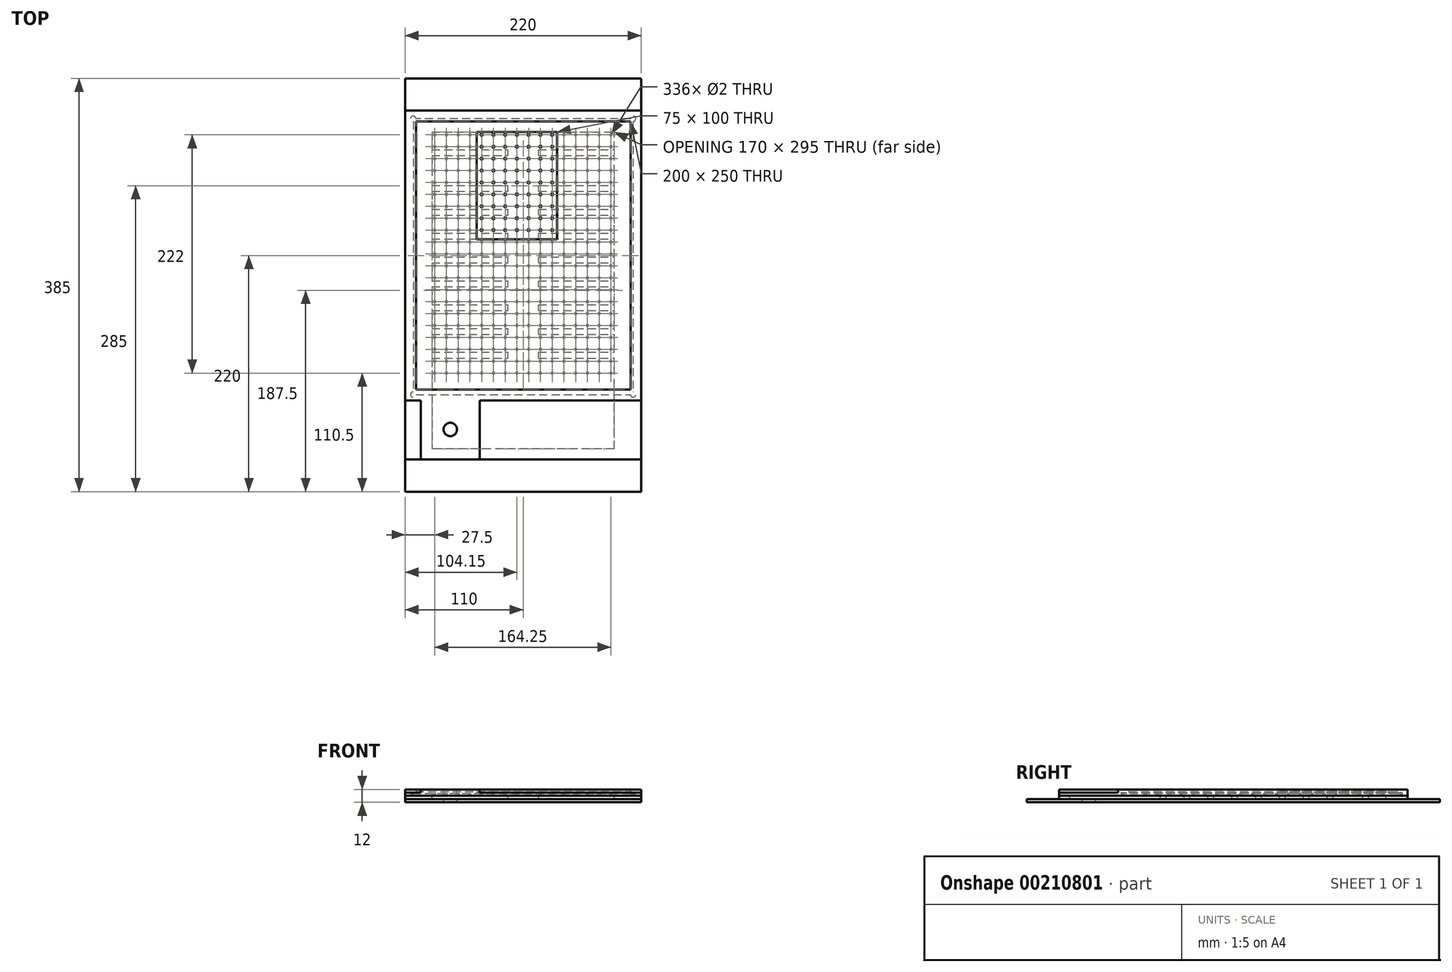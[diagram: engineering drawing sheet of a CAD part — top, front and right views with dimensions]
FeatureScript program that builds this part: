
annotation { "Feature Type Name" : "Feature", "Feature Type Description" : "" }
export const myFeature = defineFeature(function(context is Context, id is Id, definition is map)
    precondition{}
    {
        {
            var Q0;
            Q0=qCreatedBy(makeId("Top.planeOp"),FACE);
            var sketch = newSketch(context, id + "F0", { "sketchPlane" : qUnion([Q0])});
            skLineSegment(sketch, "E0.bottom", {"start": v(0, 0) * mm, "end": v(200, 0) * mm});
            skLineSegment(sketch, "E0.top", {"start": v(0, 250) * mm, "end": v(200, 250) * mm});
            skLineSegment(sketch, "E0.left", {"start": v(0, 0) * mm, "end": v(0, 250) * mm});
            skLineSegment(sketch, "E0.right", {"start": v(200, 0) * mm, "end": v(200, 250) * mm});
            skLineSegment(sketch, "E1.0", {"start": v(-10, -10) * mm, "end": v(-10, 260) * mm});
            skLineSegment(sketch, "E1.1", {"start": v(-10, -10) * mm, "end": v(210, -10) * mm});
            skLineSegment(sketch, "E1.2", {"start": v(210, -10) * mm, "end": v(210, 260) * mm});
            skLineSegment(sketch, "E1.3", {"start": v(-10, 260) * mm, "end": v(210, 260) * mm});
            skSolve(sketch);
        }
        {
            var Q0;
            Q0=makeQuery(id+"F0.imprint","IMPRINT",FACE,{"disambiguationData":[TD([[makeQuery(id+"F0.imprint","IMPRINT",EDGE,{"derivedFrom":sQuery(id+"F0.wireOp",EDGE,"E0.bottom")}),-1.0]])]});
            extrude(context, id + "F1", {"entities" : qUnion([Q0]), "depth" : 3 * mm});
        }
        {
            var Q0;
            Q0=qCreatedBy(makeId("Top.planeOp"),FACE);
            var sketch = newSketch(context, id + "F2", { "sketchPlane" : qUnion([Q0])});
            skLineSegment(sketch, "E2.0", {"start": v(-10, 260) * mm, "end": v(210, 260) * mm});
            skLineSegment(sketch, "E3", {"start": v(210, 260) * mm, "end": v(210, -65) * mm});
            skLineSegment(sketch, "E4", {"start": v(210, -65) * mm, "end": v(-10, -65) * mm});
            skLineSegment(sketch, "E5", {"start": v(-10, -65) * mm, "end": v(-10, 260) * mm});
            skLineSegment(sketch, "E6.bottom", {"start": v(15, 240) * mm, "end": v(185, 240) * mm, "construction": true});
            skLineSegment(sketch, "E6.top", {"start": v(15, 10) * mm, "end": v(185, 10) * mm, "construction": true});
            skLineSegment(sketch, "E6.left", {"start": v(15, 240) * mm, "end": v(15, 10) * mm, "construction": true});
            skLineSegment(sketch, "E6.right", {"start": v(185, 240) * mm, "end": v(185, 10) * mm, "construction": true});
            skCircle(sketch, "E7", {"center": v(17.5, 237.5) * mm, "radius": 2.5 * mm});
            skCircle(sketch, "E8.0.1.0", {"center": v(17.5, 226.4) * mm, "radius": 2.5 * mm});
            skCircle(sketch, "E8.0.2.0", {"center": v(17.5, 215.3) * mm, "radius": 2.5 * mm});
            skCircle(sketch, "E8.0.3.0", {"center": v(17.5, 204.2) * mm, "radius": 2.5 * mm});
            skCircle(sketch, "E8.0.4.0", {"center": v(17.5, 193.1) * mm, "radius": 2.5 * mm});
            skCircle(sketch, "E8.0.5.0", {"center": v(17.5, 182) * mm, "radius": 2.5 * mm});
            skCircle(sketch, "E8.0.6.0", {"center": v(17.5, 170.9) * mm, "radius": 2.5 * mm});
            skCircle(sketch, "E8.0.7.0", {"center": v(17.5, 159.8) * mm, "radius": 2.5 * mm});
            skCircle(sketch, "E8.0.8.0", {"center": v(17.5, 148.7) * mm, "radius": 2.5 * mm});
            skCircle(sketch, "E8.0.9.0", {"center": v(17.5, 137.6) * mm, "radius": 2.5 * mm});
            skCircle(sketch, "E8.0.10.0", {"center": v(17.5, 126.5) * mm, "radius": 2.5 * mm});
            skCircle(sketch, "E8.0.11.0", {"center": v(17.5, 115.4) * mm, "radius": 2.5 * mm});
            skCircle(sketch, "E8.0.12.0", {"center": v(17.5, 104.3) * mm, "radius": 2.5 * mm});
            skCircle(sketch, "E8.0.13.0", {"center": v(17.5, 93.2) * mm, "radius": 2.5 * mm});
            skCircle(sketch, "E8.0.14.0", {"center": v(17.5, 82.1) * mm, "radius": 2.5 * mm});
            skCircle(sketch, "E8.0.15.0", {"center": v(17.5, 71) * mm, "radius": 2.5 * mm});
            skCircle(sketch, "E8.0.16.0", {"center": v(17.5, 59.9) * mm, "radius": 2.5 * mm});
            skCircle(sketch, "E8.0.17.0", {"center": v(17.5, 48.8) * mm, "radius": 2.5 * mm});
            skCircle(sketch, "E8.0.18.0", {"center": v(17.5, 37.7) * mm, "radius": 2.5 * mm});
            skCircle(sketch, "E8.0.19.0", {"center": v(17.5, 26.6) * mm, "radius": 2.5 * mm});
            skCircle(sketch, "E8.1.0.0", {"center": v(28.45, 237.5) * mm, "radius": 2.5 * mm});
            skCircle(sketch, "E8.1.1.0", {"center": v(28.45, 226.4) * mm, "radius": 2.5 * mm});
            skCircle(sketch, "E8.1.2.0", {"center": v(28.45, 215.3) * mm, "radius": 2.5 * mm});
            skCircle(sketch, "E8.1.3.0", {"center": v(28.45, 204.2) * mm, "radius": 2.5 * mm});
            skCircle(sketch, "E8.1.4.0", {"center": v(28.45, 193.1) * mm, "radius": 2.5 * mm});
            skCircle(sketch, "E8.1.5.0", {"center": v(28.45, 182) * mm, "radius": 2.5 * mm});
            skCircle(sketch, "E8.1.6.0", {"center": v(28.45, 170.9) * mm, "radius": 2.5 * mm});
            skCircle(sketch, "E8.1.7.0", {"center": v(28.45, 159.8) * mm, "radius": 2.5 * mm});
            skCircle(sketch, "E8.1.8.0", {"center": v(28.45, 148.7) * mm, "radius": 2.5 * mm});
            skCircle(sketch, "E8.1.9.0", {"center": v(28.45, 137.6) * mm, "radius": 2.5 * mm});
            skCircle(sketch, "E8.1.10.0", {"center": v(28.45, 126.5) * mm, "radius": 2.5 * mm});
            skCircle(sketch, "E8.1.11.0", {"center": v(28.45, 115.4) * mm, "radius": 2.5 * mm});
            skCircle(sketch, "E8.1.12.0", {"center": v(28.45, 104.3) * mm, "radius": 2.5 * mm});
            skCircle(sketch, "E8.1.13.0", {"center": v(28.45, 93.2) * mm, "radius": 2.5 * mm});
            skCircle(sketch, "E8.1.14.0", {"center": v(28.45, 82.1) * mm, "radius": 2.5 * mm});
            skCircle(sketch, "E8.1.15.0", {"center": v(28.45, 71) * mm, "radius": 2.5 * mm});
            skCircle(sketch, "E8.1.16.0", {"center": v(28.45, 59.9) * mm, "radius": 2.5 * mm});
            skCircle(sketch, "E8.1.17.0", {"center": v(28.45, 48.8) * mm, "radius": 2.5 * mm});
            skCircle(sketch, "E8.1.18.0", {"center": v(28.45, 37.7) * mm, "radius": 2.5 * mm});
            skCircle(sketch, "E8.1.19.0", {"center": v(28.45, 26.6) * mm, "radius": 2.5 * mm});
            skCircle(sketch, "E8.2.0.0", {"center": v(39.4, 237.5) * mm, "radius": 2.5 * mm});
            skCircle(sketch, "E8.2.1.0", {"center": v(39.4, 226.4) * mm, "radius": 2.5 * mm});
            skCircle(sketch, "E8.2.2.0", {"center": v(39.4, 215.3) * mm, "radius": 2.5 * mm});
            skCircle(sketch, "E8.2.3.0", {"center": v(39.4, 204.2) * mm, "radius": 2.5 * mm});
            skCircle(sketch, "E8.2.4.0", {"center": v(39.4, 193.1) * mm, "radius": 2.5 * mm});
            skCircle(sketch, "E8.2.5.0", {"center": v(39.4, 182) * mm, "radius": 2.5 * mm});
            skCircle(sketch, "E8.2.6.0", {"center": v(39.4, 170.9) * mm, "radius": 2.5 * mm});
            skCircle(sketch, "E8.2.7.0", {"center": v(39.4, 159.8) * mm, "radius": 2.5 * mm});
            skCircle(sketch, "E8.2.8.0", {"center": v(39.4, 148.7) * mm, "radius": 2.5 * mm});
            skCircle(sketch, "E8.2.9.0", {"center": v(39.4, 137.6) * mm, "radius": 2.5 * mm});
            skCircle(sketch, "E8.2.10.0", {"center": v(39.4, 126.5) * mm, "radius": 2.5 * mm});
            skCircle(sketch, "E8.2.11.0", {"center": v(39.4, 115.4) * mm, "radius": 2.5 * mm});
            skCircle(sketch, "E8.2.12.0", {"center": v(39.4, 104.3) * mm, "radius": 2.5 * mm});
            skCircle(sketch, "E8.2.13.0", {"center": v(39.4, 93.2) * mm, "radius": 2.5 * mm});
            skCircle(sketch, "E8.2.14.0", {"center": v(39.4, 82.1) * mm, "radius": 2.5 * mm});
            skCircle(sketch, "E8.2.15.0", {"center": v(39.4, 71) * mm, "radius": 2.5 * mm});
            skCircle(sketch, "E8.2.16.0", {"center": v(39.4, 59.9) * mm, "radius": 2.5 * mm});
            skCircle(sketch, "E8.2.17.0", {"center": v(39.4, 48.8) * mm, "radius": 2.5 * mm});
            skCircle(sketch, "E8.2.18.0", {"center": v(39.4, 37.7) * mm, "radius": 2.5 * mm});
            skCircle(sketch, "E8.2.19.0", {"center": v(39.4, 26.6) * mm, "radius": 2.5 * mm});
            skCircle(sketch, "E8.3.0.0", {"center": v(50.35, 237.5) * mm, "radius": 2.5 * mm});
            skCircle(sketch, "E8.3.1.0", {"center": v(50.35, 226.4) * mm, "radius": 2.5 * mm});
            skCircle(sketch, "E8.3.2.0", {"center": v(50.35, 215.3) * mm, "radius": 2.5 * mm});
            skCircle(sketch, "E8.3.3.0", {"center": v(50.35, 204.2) * mm, "radius": 2.5 * mm});
            skCircle(sketch, "E8.3.4.0", {"center": v(50.35, 193.1) * mm, "radius": 2.5 * mm});
            skCircle(sketch, "E8.3.5.0", {"center": v(50.35, 182) * mm, "radius": 2.5 * mm});
            skCircle(sketch, "E8.3.6.0", {"center": v(50.35, 170.9) * mm, "radius": 2.5 * mm});
            skCircle(sketch, "E8.3.7.0", {"center": v(50.35, 159.8) * mm, "radius": 2.5 * mm});
            skCircle(sketch, "E8.3.8.0", {"center": v(50.35, 148.7) * mm, "radius": 2.5 * mm});
            skCircle(sketch, "E8.3.9.0", {"center": v(50.35, 137.6) * mm, "radius": 2.5 * mm});
            skCircle(sketch, "E8.3.10.0", {"center": v(50.35, 126.5) * mm, "radius": 2.5 * mm});
            skCircle(sketch, "E8.3.11.0", {"center": v(50.35, 115.4) * mm, "radius": 2.5 * mm});
            skCircle(sketch, "E8.3.12.0", {"center": v(50.35, 104.3) * mm, "radius": 2.5 * mm});
            skCircle(sketch, "E8.3.13.0", {"center": v(50.35, 93.2) * mm, "radius": 2.5 * mm});
            skCircle(sketch, "E8.3.14.0", {"center": v(50.35, 82.1) * mm, "radius": 2.5 * mm});
            skCircle(sketch, "E8.3.15.0", {"center": v(50.35, 71) * mm, "radius": 2.5 * mm});
            skCircle(sketch, "E8.3.16.0", {"center": v(50.35, 59.9) * mm, "radius": 2.5 * mm});
            skCircle(sketch, "E8.3.17.0", {"center": v(50.35, 48.8) * mm, "radius": 2.5 * mm});
            skCircle(sketch, "E8.3.18.0", {"center": v(50.35, 37.7) * mm, "radius": 2.5 * mm});
            skCircle(sketch, "E8.3.19.0", {"center": v(50.35, 26.6) * mm, "radius": 2.5 * mm});
            skCircle(sketch, "E8.4.0.0", {"center": v(61.3, 237.5) * mm, "radius": 2.5 * mm});
            skCircle(sketch, "E8.4.1.0", {"center": v(61.3, 226.4) * mm, "radius": 2.5 * mm});
            skCircle(sketch, "E8.4.2.0", {"center": v(61.3, 215.3) * mm, "radius": 2.5 * mm});
            skCircle(sketch, "E8.4.3.0", {"center": v(61.3, 204.2) * mm, "radius": 2.5 * mm});
            skCircle(sketch, "E8.4.4.0", {"center": v(61.3, 193.1) * mm, "radius": 2.5 * mm});
            skCircle(sketch, "E8.4.5.0", {"center": v(61.3, 182) * mm, "radius": 2.5 * mm});
            skCircle(sketch, "E8.4.6.0", {"center": v(61.3, 170.9) * mm, "radius": 2.5 * mm});
            skCircle(sketch, "E8.4.7.0", {"center": v(61.3, 159.8) * mm, "radius": 2.5 * mm});
            skCircle(sketch, "E8.4.8.0", {"center": v(61.3, 148.7) * mm, "radius": 2.5 * mm});
            skCircle(sketch, "E8.4.9.0", {"center": v(61.3, 137.6) * mm, "radius": 2.5 * mm});
            skCircle(sketch, "E8.4.10.0", {"center": v(61.3, 126.5) * mm, "radius": 2.5 * mm});
            skCircle(sketch, "E8.4.11.0", {"center": v(61.3, 115.4) * mm, "radius": 2.5 * mm});
            skCircle(sketch, "E8.4.12.0", {"center": v(61.3, 104.3) * mm, "radius": 2.5 * mm});
            skCircle(sketch, "E8.4.13.0", {"center": v(61.3, 93.2) * mm, "radius": 2.5 * mm});
            skCircle(sketch, "E8.4.14.0", {"center": v(61.3, 82.1) * mm, "radius": 2.5 * mm});
            skCircle(sketch, "E8.4.15.0", {"center": v(61.3, 71) * mm, "radius": 2.5 * mm});
            skCircle(sketch, "E8.4.16.0", {"center": v(61.3, 59.9) * mm, "radius": 2.5 * mm});
            skCircle(sketch, "E8.4.17.0", {"center": v(61.3, 48.8) * mm, "radius": 2.5 * mm});
            skCircle(sketch, "E8.4.18.0", {"center": v(61.3, 37.7) * mm, "radius": 2.5 * mm});
            skCircle(sketch, "E8.4.19.0", {"center": v(61.3, 26.6) * mm, "radius": 2.5 * mm});
            skCircle(sketch, "E8.5.0.0", {"center": v(72.25, 237.5) * mm, "radius": 2.5 * mm});
            skCircle(sketch, "E8.5.1.0", {"center": v(72.25, 226.4) * mm, "radius": 2.5 * mm});
            skCircle(sketch, "E8.5.2.0", {"center": v(72.25, 215.3) * mm, "radius": 2.5 * mm});
            skCircle(sketch, "E8.5.3.0", {"center": v(72.25, 204.2) * mm, "radius": 2.5 * mm});
            skCircle(sketch, "E8.5.4.0", {"center": v(72.25, 193.1) * mm, "radius": 2.5 * mm});
            skCircle(sketch, "E8.5.5.0", {"center": v(72.25, 182) * mm, "radius": 2.5 * mm});
            skCircle(sketch, "E8.5.6.0", {"center": v(72.25, 170.9) * mm, "radius": 2.5 * mm});
            skCircle(sketch, "E8.5.7.0", {"center": v(72.25, 159.8) * mm, "radius": 2.5 * mm});
            skCircle(sketch, "E8.5.8.0", {"center": v(72.25, 148.7) * mm, "radius": 2.5 * mm});
            skCircle(sketch, "E8.5.9.0", {"center": v(72.25, 137.6) * mm, "radius": 2.5 * mm});
            skCircle(sketch, "E8.5.10.0", {"center": v(72.25, 126.5) * mm, "radius": 2.5 * mm});
            skCircle(sketch, "E8.5.11.0", {"center": v(72.25, 115.4) * mm, "radius": 2.5 * mm});
            skCircle(sketch, "E8.5.12.0", {"center": v(72.25, 104.3) * mm, "radius": 2.5 * mm});
            skCircle(sketch, "E8.5.13.0", {"center": v(72.25, 93.2) * mm, "radius": 2.5 * mm});
            skCircle(sketch, "E8.5.14.0", {"center": v(72.25, 82.1) * mm, "radius": 2.5 * mm});
            skCircle(sketch, "E8.5.15.0", {"center": v(72.25, 71) * mm, "radius": 2.5 * mm});
            skCircle(sketch, "E8.5.16.0", {"center": v(72.25, 59.9) * mm, "radius": 2.5 * mm});
            skCircle(sketch, "E8.5.17.0", {"center": v(72.25, 48.8) * mm, "radius": 2.5 * mm});
            skCircle(sketch, "E8.5.18.0", {"center": v(72.25, 37.7) * mm, "radius": 2.5 * mm});
            skCircle(sketch, "E8.5.19.0", {"center": v(72.25, 26.6) * mm, "radius": 2.5 * mm});
            skCircle(sketch, "E8.6.0.0", {"center": v(83.2, 237.5) * mm, "radius": 2.5 * mm});
            skCircle(sketch, "E8.6.1.0", {"center": v(83.2, 226.4) * mm, "radius": 2.5 * mm});
            skCircle(sketch, "E8.6.2.0", {"center": v(83.2, 215.3) * mm, "radius": 2.5 * mm});
            skCircle(sketch, "E8.6.3.0", {"center": v(83.2, 204.2) * mm, "radius": 2.5 * mm});
            skCircle(sketch, "E8.6.4.0", {"center": v(83.2, 193.1) * mm, "radius": 2.5 * mm});
            skCircle(sketch, "E8.6.5.0", {"center": v(83.2, 182) * mm, "radius": 2.5 * mm});
            skCircle(sketch, "E8.6.6.0", {"center": v(83.2, 170.9) * mm, "radius": 2.5 * mm});
            skCircle(sketch, "E8.6.7.0", {"center": v(83.2, 159.8) * mm, "radius": 2.5 * mm});
            skCircle(sketch, "E8.6.8.0", {"center": v(83.2, 148.7) * mm, "radius": 2.5 * mm});
            skCircle(sketch, "E8.6.9.0", {"center": v(83.2, 137.6) * mm, "radius": 2.5 * mm});
            skCircle(sketch, "E8.6.10.0", {"center": v(83.2, 126.5) * mm, "radius": 2.5 * mm});
            skCircle(sketch, "E8.6.11.0", {"center": v(83.2, 115.4) * mm, "radius": 2.5 * mm});
            skCircle(sketch, "E8.6.12.0", {"center": v(83.2, 104.3) * mm, "radius": 2.5 * mm});
            skCircle(sketch, "E8.6.13.0", {"center": v(83.2, 93.2) * mm, "radius": 2.5 * mm});
            skCircle(sketch, "E8.6.14.0", {"center": v(83.2, 82.1) * mm, "radius": 2.5 * mm});
            skCircle(sketch, "E8.6.15.0", {"center": v(83.2, 71) * mm, "radius": 2.5 * mm});
            skCircle(sketch, "E8.6.16.0", {"center": v(83.2, 59.9) * mm, "radius": 2.5 * mm});
            skCircle(sketch, "E8.6.17.0", {"center": v(83.2, 48.8) * mm, "radius": 2.5 * mm});
            skCircle(sketch, "E8.6.18.0", {"center": v(83.2, 37.7) * mm, "radius": 2.5 * mm});
            skCircle(sketch, "E8.6.19.0", {"center": v(83.2, 26.6) * mm, "radius": 2.5 * mm});
            skCircle(sketch, "E8.7.0.0", {"center": v(94.15, 237.5) * mm, "radius": 2.5 * mm});
            skCircle(sketch, "E8.7.1.0", {"center": v(94.15, 226.4) * mm, "radius": 2.5 * mm});
            skCircle(sketch, "E8.7.2.0", {"center": v(94.15, 215.3) * mm, "radius": 2.5 * mm});
            skCircle(sketch, "E8.7.3.0", {"center": v(94.15, 204.2) * mm, "radius": 2.5 * mm});
            skCircle(sketch, "E8.7.4.0", {"center": v(94.15, 193.1) * mm, "radius": 2.5 * mm});
            skCircle(sketch, "E8.7.5.0", {"center": v(94.15, 182) * mm, "radius": 2.5 * mm});
            skCircle(sketch, "E8.7.6.0", {"center": v(94.15, 170.9) * mm, "radius": 2.5 * mm});
            skCircle(sketch, "E8.7.7.0", {"center": v(94.15, 159.8) * mm, "radius": 2.5 * mm});
            skCircle(sketch, "E8.7.8.0", {"center": v(94.15, 148.7) * mm, "radius": 2.5 * mm});
            skCircle(sketch, "E8.7.9.0", {"center": v(94.15, 137.6) * mm, "radius": 2.5 * mm});
            skCircle(sketch, "E8.7.10.0", {"center": v(94.15, 126.5) * mm, "radius": 2.5 * mm});
            skCircle(sketch, "E8.7.11.0", {"center": v(94.15, 115.4) * mm, "radius": 2.5 * mm});
            skCircle(sketch, "E8.7.12.0", {"center": v(94.15, 104.3) * mm, "radius": 2.5 * mm});
            skCircle(sketch, "E8.7.13.0", {"center": v(94.15, 93.2) * mm, "radius": 2.5 * mm});
            skCircle(sketch, "E8.7.14.0", {"center": v(94.15, 82.1) * mm, "radius": 2.5 * mm});
            skCircle(sketch, "E8.7.15.0", {"center": v(94.15, 71) * mm, "radius": 2.5 * mm});
            skCircle(sketch, "E8.7.16.0", {"center": v(94.15, 59.9) * mm, "radius": 2.5 * mm});
            skCircle(sketch, "E8.7.17.0", {"center": v(94.15, 48.8) * mm, "radius": 2.5 * mm});
            skCircle(sketch, "E8.7.18.0", {"center": v(94.15, 37.7) * mm, "radius": 2.5 * mm});
            skCircle(sketch, "E8.7.19.0", {"center": v(94.15, 26.6) * mm, "radius": 2.5 * mm});
            skCircle(sketch, "E8.8.0.0", {"center": v(105.1, 237.5) * mm, "radius": 2.5 * mm});
            skCircle(sketch, "E8.8.1.0", {"center": v(105.1, 226.4) * mm, "radius": 2.5 * mm});
            skCircle(sketch, "E8.8.2.0", {"center": v(105.1, 215.3) * mm, "radius": 2.5 * mm});
            skCircle(sketch, "E8.8.3.0", {"center": v(105.1, 204.2) * mm, "radius": 2.5 * mm});
            skCircle(sketch, "E8.8.4.0", {"center": v(105.1, 193.1) * mm, "radius": 2.5 * mm});
            skCircle(sketch, "E8.8.5.0", {"center": v(105.1, 182) * mm, "radius": 2.5 * mm});
            skCircle(sketch, "E8.8.6.0", {"center": v(105.1, 170.9) * mm, "radius": 2.5 * mm});
            skCircle(sketch, "E8.8.7.0", {"center": v(105.1, 159.8) * mm, "radius": 2.5 * mm});
            skCircle(sketch, "E8.8.8.0", {"center": v(105.1, 148.7) * mm, "radius": 2.5 * mm});
            skCircle(sketch, "E8.8.9.0", {"center": v(105.1, 137.6) * mm, "radius": 2.5 * mm});
            skCircle(sketch, "E8.8.10.0", {"center": v(105.1, 126.5) * mm, "radius": 2.5 * mm});
            skCircle(sketch, "E8.8.11.0", {"center": v(105.1, 115.4) * mm, "radius": 2.5 * mm});
            skCircle(sketch, "E8.8.12.0", {"center": v(105.1, 104.3) * mm, "radius": 2.5 * mm});
            skCircle(sketch, "E8.8.13.0", {"center": v(105.1, 93.2) * mm, "radius": 2.5 * mm});
            skCircle(sketch, "E8.8.14.0", {"center": v(105.1, 82.1) * mm, "radius": 2.5 * mm});
            skCircle(sketch, "E8.8.15.0", {"center": v(105.1, 71) * mm, "radius": 2.5 * mm});
            skCircle(sketch, "E8.8.16.0", {"center": v(105.1, 59.9) * mm, "radius": 2.5 * mm});
            skCircle(sketch, "E8.8.17.0", {"center": v(105.1, 48.8) * mm, "radius": 2.5 * mm});
            skCircle(sketch, "E8.8.18.0", {"center": v(105.1, 37.7) * mm, "radius": 2.5 * mm});
            skCircle(sketch, "E8.8.19.0", {"center": v(105.1, 26.6) * mm, "radius": 2.5 * mm});
            skCircle(sketch, "E8.9.0.0", {"center": v(116.05, 237.5) * mm, "radius": 2.5 * mm});
            skCircle(sketch, "E8.9.1.0", {"center": v(116.05, 226.4) * mm, "radius": 2.5 * mm});
            skCircle(sketch, "E8.9.2.0", {"center": v(116.05, 215.3) * mm, "radius": 2.5 * mm});
            skCircle(sketch, "E8.9.3.0", {"center": v(116.05, 204.2) * mm, "radius": 2.5 * mm});
            skCircle(sketch, "E8.9.4.0", {"center": v(116.05, 193.1) * mm, "radius": 2.5 * mm});
            skCircle(sketch, "E8.9.5.0", {"center": v(116.05, 182) * mm, "radius": 2.5 * mm});
            skCircle(sketch, "E8.9.6.0", {"center": v(116.05, 170.9) * mm, "radius": 2.5 * mm});
            skCircle(sketch, "E8.9.7.0", {"center": v(116.05, 159.8) * mm, "radius": 2.5 * mm});
            skCircle(sketch, "E8.9.8.0", {"center": v(116.05, 148.7) * mm, "radius": 2.5 * mm});
            skCircle(sketch, "E8.9.9.0", {"center": v(116.05, 137.6) * mm, "radius": 2.5 * mm});
            skCircle(sketch, "E8.9.10.0", {"center": v(116.05, 126.5) * mm, "radius": 2.5 * mm});
            skCircle(sketch, "E8.9.11.0", {"center": v(116.05, 115.4) * mm, "radius": 2.5 * mm});
            skCircle(sketch, "E8.9.12.0", {"center": v(116.05, 104.3) * mm, "radius": 2.5 * mm});
            skCircle(sketch, "E8.9.13.0", {"center": v(116.05, 93.2) * mm, "radius": 2.5 * mm});
            skCircle(sketch, "E8.9.14.0", {"center": v(116.05, 82.1) * mm, "radius": 2.5 * mm});
            skCircle(sketch, "E8.9.15.0", {"center": v(116.05, 71) * mm, "radius": 2.5 * mm});
            skCircle(sketch, "E8.9.16.0", {"center": v(116.05, 59.9) * mm, "radius": 2.5 * mm});
            skCircle(sketch, "E8.9.17.0", {"center": v(116.05, 48.8) * mm, "radius": 2.5 * mm});
            skCircle(sketch, "E8.9.18.0", {"center": v(116.05, 37.7) * mm, "radius": 2.5 * mm});
            skCircle(sketch, "E8.9.19.0", {"center": v(116.05, 26.6) * mm, "radius": 2.5 * mm});
            skCircle(sketch, "E8.10.0.0", {"center": v(127, 237.5) * mm, "radius": 2.5 * mm});
            skCircle(sketch, "E8.10.1.0", {"center": v(127, 226.4) * mm, "radius": 2.5 * mm});
            skCircle(sketch, "E8.10.2.0", {"center": v(127, 215.3) * mm, "radius": 2.5 * mm});
            skCircle(sketch, "E8.10.3.0", {"center": v(127, 204.2) * mm, "radius": 2.5 * mm});
            skCircle(sketch, "E8.10.4.0", {"center": v(127, 193.1) * mm, "radius": 2.5 * mm});
            skCircle(sketch, "E8.10.5.0", {"center": v(127, 182) * mm, "radius": 2.5 * mm});
            skCircle(sketch, "E8.10.6.0", {"center": v(127, 170.9) * mm, "radius": 2.5 * mm});
            skCircle(sketch, "E8.10.7.0", {"center": v(127, 159.8) * mm, "radius": 2.5 * mm});
            skCircle(sketch, "E8.10.8.0", {"center": v(127, 148.7) * mm, "radius": 2.5 * mm});
            skCircle(sketch, "E8.10.9.0", {"center": v(127, 137.6) * mm, "radius": 2.5 * mm});
            skCircle(sketch, "E8.10.10.0", {"center": v(127, 126.5) * mm, "radius": 2.5 * mm});
            skCircle(sketch, "E8.10.11.0", {"center": v(127, 115.4) * mm, "radius": 2.5 * mm});
            skCircle(sketch, "E8.10.12.0", {"center": v(127, 104.3) * mm, "radius": 2.5 * mm});
            skCircle(sketch, "E8.10.13.0", {"center": v(127, 93.2) * mm, "radius": 2.5 * mm});
            skCircle(sketch, "E8.10.14.0", {"center": v(127, 82.1) * mm, "radius": 2.5 * mm});
            skCircle(sketch, "E8.10.15.0", {"center": v(127, 71) * mm, "radius": 2.5 * mm});
            skCircle(sketch, "E8.10.16.0", {"center": v(127, 59.9) * mm, "radius": 2.5 * mm});
            skCircle(sketch, "E8.10.17.0", {"center": v(127, 48.8) * mm, "radius": 2.5 * mm});
            skCircle(sketch, "E8.10.18.0", {"center": v(127, 37.7) * mm, "radius": 2.5 * mm});
            skCircle(sketch, "E8.10.19.0", {"center": v(127, 26.6) * mm, "radius": 2.5 * mm});
            skCircle(sketch, "E8.11.0.0", {"center": v(137.95, 237.5) * mm, "radius": 2.5 * mm});
            skCircle(sketch, "E8.11.1.0", {"center": v(137.95, 226.4) * mm, "radius": 2.5 * mm});
            skCircle(sketch, "E8.11.2.0", {"center": v(137.95, 215.3) * mm, "radius": 2.5 * mm});
            skCircle(sketch, "E8.11.3.0", {"center": v(137.95, 204.2) * mm, "radius": 2.5 * mm});
            skCircle(sketch, "E8.11.4.0", {"center": v(137.95, 193.1) * mm, "radius": 2.5 * mm});
            skCircle(sketch, "E8.11.5.0", {"center": v(137.95, 182) * mm, "radius": 2.5 * mm});
            skCircle(sketch, "E8.11.6.0", {"center": v(137.95, 170.9) * mm, "radius": 2.5 * mm});
            skCircle(sketch, "E8.11.7.0", {"center": v(137.95, 159.8) * mm, "radius": 2.5 * mm});
            skCircle(sketch, "E8.11.8.0", {"center": v(137.95, 148.7) * mm, "radius": 2.5 * mm});
            skCircle(sketch, "E8.11.9.0", {"center": v(137.95, 137.6) * mm, "radius": 2.5 * mm});
            skCircle(sketch, "E8.11.10.0", {"center": v(137.95, 126.5) * mm, "radius": 2.5 * mm});
            skCircle(sketch, "E8.11.11.0", {"center": v(137.95, 115.4) * mm, "radius": 2.5 * mm});
            skCircle(sketch, "E8.11.12.0", {"center": v(137.95, 104.3) * mm, "radius": 2.5 * mm});
            skCircle(sketch, "E8.11.13.0", {"center": v(137.95, 93.2) * mm, "radius": 2.5 * mm});
            skCircle(sketch, "E8.11.14.0", {"center": v(137.95, 82.1) * mm, "radius": 2.5 * mm});
            skCircle(sketch, "E8.11.15.0", {"center": v(137.95, 71) * mm, "radius": 2.5 * mm});
            skCircle(sketch, "E8.11.16.0", {"center": v(137.95, 59.9) * mm, "radius": 2.5 * mm});
            skCircle(sketch, "E8.11.17.0", {"center": v(137.95, 48.8) * mm, "radius": 2.5 * mm});
            skCircle(sketch, "E8.11.18.0", {"center": v(137.95, 37.7) * mm, "radius": 2.5 * mm});
            skCircle(sketch, "E8.11.19.0", {"center": v(137.95, 26.6) * mm, "radius": 2.5 * mm});
            skCircle(sketch, "E8.12.0.0", {"center": v(148.9, 237.5) * mm, "radius": 2.5 * mm});
            skCircle(sketch, "E8.12.1.0", {"center": v(148.9, 226.4) * mm, "radius": 2.5 * mm});
            skCircle(sketch, "E8.12.2.0", {"center": v(148.9, 215.3) * mm, "radius": 2.5 * mm});
            skCircle(sketch, "E8.12.3.0", {"center": v(148.9, 204.2) * mm, "radius": 2.5 * mm});
            skCircle(sketch, "E8.12.4.0", {"center": v(148.9, 193.1) * mm, "radius": 2.5 * mm});
            skCircle(sketch, "E8.12.5.0", {"center": v(148.9, 182) * mm, "radius": 2.5 * mm});
            skCircle(sketch, "E8.12.6.0", {"center": v(148.9, 170.9) * mm, "radius": 2.5 * mm});
            skCircle(sketch, "E8.12.7.0", {"center": v(148.9, 159.8) * mm, "radius": 2.5 * mm});
            skCircle(sketch, "E8.12.8.0", {"center": v(148.9, 148.7) * mm, "radius": 2.5 * mm});
            skCircle(sketch, "E8.12.9.0", {"center": v(148.9, 137.6) * mm, "radius": 2.5 * mm});
            skCircle(sketch, "E8.12.10.0", {"center": v(148.9, 126.5) * mm, "radius": 2.5 * mm});
            skCircle(sketch, "E8.12.11.0", {"center": v(148.9, 115.4) * mm, "radius": 2.5 * mm});
            skCircle(sketch, "E8.12.12.0", {"center": v(148.9, 104.3) * mm, "radius": 2.5 * mm});
            skCircle(sketch, "E8.12.13.0", {"center": v(148.9, 93.2) * mm, "radius": 2.5 * mm});
            skCircle(sketch, "E8.12.14.0", {"center": v(148.9, 82.1) * mm, "radius": 2.5 * mm});
            skCircle(sketch, "E8.12.15.0", {"center": v(148.9, 71) * mm, "radius": 2.5 * mm});
            skCircle(sketch, "E8.12.16.0", {"center": v(148.9, 59.9) * mm, "radius": 2.5 * mm});
            skCircle(sketch, "E8.12.17.0", {"center": v(148.9, 48.8) * mm, "radius": 2.5 * mm});
            skCircle(sketch, "E8.12.18.0", {"center": v(148.9, 37.7) * mm, "radius": 2.5 * mm});
            skCircle(sketch, "E8.12.19.0", {"center": v(148.9, 26.6) * mm, "radius": 2.5 * mm});
            skCircle(sketch, "E8.13.0.0", {"center": v(159.85, 237.5) * mm, "radius": 2.5 * mm});
            skCircle(sketch, "E8.13.1.0", {"center": v(159.85, 226.4) * mm, "radius": 2.5 * mm});
            skCircle(sketch, "E8.13.2.0", {"center": v(159.85, 215.3) * mm, "radius": 2.5 * mm});
            skCircle(sketch, "E8.13.3.0", {"center": v(159.85, 204.2) * mm, "radius": 2.5 * mm});
            skCircle(sketch, "E8.13.4.0", {"center": v(159.85, 193.1) * mm, "radius": 2.5 * mm});
            skCircle(sketch, "E8.13.5.0", {"center": v(159.85, 182) * mm, "radius": 2.5 * mm});
            skCircle(sketch, "E8.13.6.0", {"center": v(159.85, 170.9) * mm, "radius": 2.5 * mm});
            skCircle(sketch, "E8.13.7.0", {"center": v(159.85, 159.8) * mm, "radius": 2.5 * mm});
            skCircle(sketch, "E8.13.8.0", {"center": v(159.85, 148.7) * mm, "radius": 2.5 * mm});
            skCircle(sketch, "E8.13.9.0", {"center": v(159.85, 137.6) * mm, "radius": 2.5 * mm});
            skCircle(sketch, "E8.13.10.0", {"center": v(159.85, 126.5) * mm, "radius": 2.5 * mm});
            skCircle(sketch, "E8.13.11.0", {"center": v(159.85, 115.4) * mm, "radius": 2.5 * mm});
            skCircle(sketch, "E8.13.12.0", {"center": v(159.85, 104.3) * mm, "radius": 2.5 * mm});
            skCircle(sketch, "E8.13.13.0", {"center": v(159.85, 93.2) * mm, "radius": 2.5 * mm});
            skCircle(sketch, "E8.13.14.0", {"center": v(159.85, 82.1) * mm, "radius": 2.5 * mm});
            skCircle(sketch, "E8.13.15.0", {"center": v(159.85, 71) * mm, "radius": 2.5 * mm});
            skCircle(sketch, "E8.13.16.0", {"center": v(159.85, 59.9) * mm, "radius": 2.5 * mm});
            skCircle(sketch, "E8.13.17.0", {"center": v(159.85, 48.8) * mm, "radius": 2.5 * mm});
            skCircle(sketch, "E8.13.18.0", {"center": v(159.85, 37.7) * mm, "radius": 2.5 * mm});
            skCircle(sketch, "E8.13.19.0", {"center": v(159.85, 26.6) * mm, "radius": 2.5 * mm});
            skCircle(sketch, "E8.14.0.0", {"center": v(170.8, 237.5) * mm, "radius": 2.5 * mm});
            skCircle(sketch, "E8.14.1.0", {"center": v(170.8, 226.4) * mm, "radius": 2.5 * mm});
            skCircle(sketch, "E8.14.2.0", {"center": v(170.8, 215.3) * mm, "radius": 2.5 * mm});
            skCircle(sketch, "E8.14.3.0", {"center": v(170.8, 204.2) * mm, "radius": 2.5 * mm});
            skCircle(sketch, "E8.14.4.0", {"center": v(170.8, 193.1) * mm, "radius": 2.5 * mm});
            skCircle(sketch, "E8.14.5.0", {"center": v(170.8, 182) * mm, "radius": 2.5 * mm});
            skCircle(sketch, "E8.14.6.0", {"center": v(170.8, 170.9) * mm, "radius": 2.5 * mm});
            skCircle(sketch, "E8.14.7.0", {"center": v(170.8, 159.8) * mm, "radius": 2.5 * mm});
            skCircle(sketch, "E8.14.8.0", {"center": v(170.8, 148.7) * mm, "radius": 2.5 * mm});
            skCircle(sketch, "E8.14.9.0", {"center": v(170.8, 137.6) * mm, "radius": 2.5 * mm});
            skCircle(sketch, "E8.14.10.0", {"center": v(170.8, 126.5) * mm, "radius": 2.5 * mm});
            skCircle(sketch, "E8.14.11.0", {"center": v(170.8, 115.4) * mm, "radius": 2.5 * mm});
            skCircle(sketch, "E8.14.12.0", {"center": v(170.8, 104.3) * mm, "radius": 2.5 * mm});
            skCircle(sketch, "E8.14.13.0", {"center": v(170.8, 93.2) * mm, "radius": 2.5 * mm});
            skCircle(sketch, "E8.14.14.0", {"center": v(170.8, 82.1) * mm, "radius": 2.5 * mm});
            skCircle(sketch, "E8.14.15.0", {"center": v(170.8, 71) * mm, "radius": 2.5 * mm});
            skCircle(sketch, "E8.14.16.0", {"center": v(170.8, 59.9) * mm, "radius": 2.5 * mm});
            skCircle(sketch, "E8.14.17.0", {"center": v(170.8, 48.8) * mm, "radius": 2.5 * mm});
            skCircle(sketch, "E8.14.18.0", {"center": v(170.8, 37.7) * mm, "radius": 2.5 * mm});
            skCircle(sketch, "E8.14.19.0", {"center": v(170.8, 26.6) * mm, "radius": 2.5 * mm});
            skLineSegment(sketch, "E8.direction1", {"start": v(17.5, 237.5) * mm, "end": v(28.45, 237.5) * mm, "construction": true});
            skLineSegment(sketch, "E8.direction2", {"start": v(17.5, 237.5) * mm, "end": v(17.5, 226.4) * mm, "construction": true});
            skCircle(sketch, "E9.0.15.0", {"center": v(181.75, 237.5) * mm, "radius": 2.5 * mm});
            skCircle(sketch, "E9.0.15.1", {"center": v(181.75, 226.4) * mm, "radius": 2.5 * mm});
            skCircle(sketch, "E9.0.15.2", {"center": v(181.75, 215.3) * mm, "radius": 2.5 * mm});
            skCircle(sketch, "E9.0.15.3", {"center": v(181.75, 204.2) * mm, "radius": 2.5 * mm});
            skCircle(sketch, "E9.0.15.4", {"center": v(181.75, 193.1) * mm, "radius": 2.5 * mm});
            skCircle(sketch, "E9.0.15.5", {"center": v(181.75, 182) * mm, "radius": 2.5 * mm});
            skCircle(sketch, "E9.0.15.6", {"center": v(181.75, 170.9) * mm, "radius": 2.5 * mm});
            skCircle(sketch, "E9.0.15.7", {"center": v(181.75, 159.8) * mm, "radius": 2.5 * mm});
            skCircle(sketch, "E9.0.15.8", {"center": v(181.75, 148.7) * mm, "radius": 2.5 * mm});
            skCircle(sketch, "E9.0.15.9", {"center": v(181.75, 137.6) * mm, "radius": 2.5 * mm});
            skCircle(sketch, "E9.0.15.10", {"center": v(181.75, 126.5) * mm, "radius": 2.5 * mm});
            skCircle(sketch, "E9.0.15.11", {"center": v(181.75, 115.4) * mm, "radius": 2.5 * mm});
            skCircle(sketch, "E9.0.15.12", {"center": v(181.75, 104.3) * mm, "radius": 2.5 * mm});
            skCircle(sketch, "E9.0.15.13", {"center": v(181.75, 93.2) * mm, "radius": 2.5 * mm});
            skCircle(sketch, "E9.0.15.14", {"center": v(181.75, 82.1) * mm, "radius": 2.5 * mm});
            skCircle(sketch, "E9.0.15.15", {"center": v(181.75, 71) * mm, "radius": 2.5 * mm});
            skCircle(sketch, "E9.0.15.16", {"center": v(181.75, 59.9) * mm, "radius": 2.5 * mm});
            skCircle(sketch, "E9.0.15.17", {"center": v(181.75, 48.8) * mm, "radius": 2.5 * mm});
            skCircle(sketch, "E9.0.15.18", {"center": v(181.75, 37.7) * mm, "radius": 2.5 * mm});
            skCircle(sketch, "E9.0.15.19", {"center": v(181.75, 26.6) * mm, "radius": 2.5 * mm});
            skCircle(sketch, "E10.0.0.20", {"center": v(17.5, 15.5) * mm, "radius": 2.5 * mm});
            skCircle(sketch, "E10.0.1.20", {"center": v(28.45, 15.5) * mm, "radius": 2.5 * mm});
            skCircle(sketch, "E10.0.2.20", {"center": v(39.4, 15.5) * mm, "radius": 2.5 * mm});
            skCircle(sketch, "E10.0.3.20", {"center": v(50.35, 15.5) * mm, "radius": 2.5 * mm});
            skCircle(sketch, "E10.0.4.20", {"center": v(61.3, 15.5) * mm, "radius": 2.5 * mm});
            skCircle(sketch, "E10.0.5.20", {"center": v(72.25, 15.5) * mm, "radius": 2.5 * mm});
            skCircle(sketch, "E10.0.6.20", {"center": v(83.2, 15.5) * mm, "radius": 2.5 * mm});
            skCircle(sketch, "E10.0.7.20", {"center": v(94.15, 15.5) * mm, "radius": 2.5 * mm});
            skCircle(sketch, "E10.0.8.20", {"center": v(105.1, 15.5) * mm, "radius": 2.5 * mm});
            skCircle(sketch, "E10.0.9.20", {"center": v(116.05, 15.5) * mm, "radius": 2.5 * mm});
            skCircle(sketch, "E10.0.10.20", {"center": v(127, 15.5) * mm, "radius": 2.5 * mm});
            skCircle(sketch, "E10.0.11.20", {"center": v(137.95, 15.5) * mm, "radius": 2.5 * mm});
            skCircle(sketch, "E10.0.12.20", {"center": v(148.9, 15.5) * mm, "radius": 2.5 * mm});
            skCircle(sketch, "E10.0.13.20", {"center": v(159.85, 15.5) * mm, "radius": 2.5 * mm});
            skCircle(sketch, "E10.0.14.20", {"center": v(170.8, 15.5) * mm, "radius": 2.5 * mm});
            skCircle(sketch, "E10.0.15.20", {"center": v(181.75, 15.5) * mm, "radius": 2.5 * mm});
            skCircle(sketch, "E11", {"center": v(32.07, -37.07) * mm, "radius": 17.07 * mm});
            skSolve(sketch);
        }
        {
            var Q0;
            Q0=makeQuery(id+"F2.imprint","IMPRINT",FACE,{"disambiguationData":[TD([[makeQuery(id+"F2.imprint","IMPRINT",EDGE,{"derivedFrom":sQuery(id+"F2.wireOp",EDGE,"E2.0")}),-1.0]])]});
            extrude(context, id + "F3", {"entities" : qUnion([Q0]), "oppositeDirection" : true, "depth" : 3 * mm});
        }
        {
            var Q0;
            Q0=qCreatedBy(makeId("Top.planeOp"),FACE);
            var sketch = newSketch(context, id + "F4", { "sketchPlane" : qUnion([Q0])});
            skLineSegment(sketch, "E12.0.0", {"start": v(-10, 260) * mm, "end": v(-10, -65) * mm});
            skLineSegment(sketch, "E12.0.1", {"start": v(-10, -65) * mm, "end": v(210, -65) * mm});
            skLineSegment(sketch, "E12.0.2", {"start": v(210, -65) * mm, "end": v(210, 260) * mm});
            skLineSegment(sketch, "E12.0.3", {"start": v(210, 260) * mm, "end": v(-10, 260) * mm});
            skCircle(sketch, "E13.0", {"center": v(32.07, -37.07) * mm, "radius": 17.07 * mm});
            skCircle(sketch, "E14", {"center": v(17.5, 237.5) * mm, "radius": 1 * mm});
            skCircle(sketch, "E15.0.1.0", {"center": v(17.5, 226.4) * mm, "radius": 1 * mm});
            skCircle(sketch, "E15.0.2.0", {"center": v(17.5, 215.3) * mm, "radius": 1 * mm});
            skCircle(sketch, "E15.0.3.0", {"center": v(17.5, 204.2) * mm, "radius": 1 * mm});
            skCircle(sketch, "E15.0.4.0", {"center": v(17.5, 193.1) * mm, "radius": 1 * mm});
            skCircle(sketch, "E15.0.5.0", {"center": v(17.5, 182) * mm, "radius": 1 * mm});
            skCircle(sketch, "E15.0.6.0", {"center": v(17.5, 170.9) * mm, "radius": 1 * mm});
            skCircle(sketch, "E15.0.7.0", {"center": v(17.5, 159.8) * mm, "radius": 1 * mm});
            skCircle(sketch, "E15.0.8.0", {"center": v(17.5, 148.7) * mm, "radius": 1 * mm});
            skCircle(sketch, "E15.0.9.0", {"center": v(17.5, 137.6) * mm, "radius": 1 * mm});
            skCircle(sketch, "E15.0.10.0", {"center": v(17.5, 126.5) * mm, "radius": 1 * mm});
            skCircle(sketch, "E15.0.11.0", {"center": v(17.5, 115.4) * mm, "radius": 1 * mm});
            skCircle(sketch, "E15.0.12.0", {"center": v(17.5, 104.3) * mm, "radius": 1 * mm});
            skCircle(sketch, "E15.0.13.0", {"center": v(17.5, 93.2) * mm, "radius": 1 * mm});
            skCircle(sketch, "E15.0.14.0", {"center": v(17.5, 82.1) * mm, "radius": 1 * mm});
            skCircle(sketch, "E15.0.15.0", {"center": v(17.5, 71) * mm, "radius": 1 * mm});
            skCircle(sketch, "E15.0.16.0", {"center": v(17.5, 59.9) * mm, "radius": 1 * mm});
            skCircle(sketch, "E15.0.17.0", {"center": v(17.5, 48.8) * mm, "radius": 1 * mm});
            skCircle(sketch, "E15.0.18.0", {"center": v(17.5, 37.7) * mm, "radius": 1 * mm});
            skCircle(sketch, "E15.0.19.0", {"center": v(17.5, 26.6) * mm, "radius": 1 * mm});
            skCircle(sketch, "E15.0.20.0", {"center": v(17.5, 15.5) * mm, "radius": 1 * mm});
            skCircle(sketch, "E15.1.0.0", {"center": v(28.45, 237.5) * mm, "radius": 1 * mm});
            skCircle(sketch, "E15.1.1.0", {"center": v(28.45, 226.4) * mm, "radius": 1 * mm});
            skCircle(sketch, "E15.1.2.0", {"center": v(28.45, 215.3) * mm, "radius": 1 * mm});
            skCircle(sketch, "E15.1.3.0", {"center": v(28.45, 204.2) * mm, "radius": 1 * mm});
            skCircle(sketch, "E15.1.4.0", {"center": v(28.45, 193.1) * mm, "radius": 1 * mm});
            skCircle(sketch, "E15.1.5.0", {"center": v(28.45, 182) * mm, "radius": 1 * mm});
            skCircle(sketch, "E15.1.6.0", {"center": v(28.45, 170.9) * mm, "radius": 1 * mm});
            skCircle(sketch, "E15.1.7.0", {"center": v(28.45, 159.8) * mm, "radius": 1 * mm});
            skCircle(sketch, "E15.1.8.0", {"center": v(28.45, 148.7) * mm, "radius": 1 * mm});
            skCircle(sketch, "E15.1.9.0", {"center": v(28.45, 137.6) * mm, "radius": 1 * mm});
            skCircle(sketch, "E15.1.10.0", {"center": v(28.45, 126.5) * mm, "radius": 1 * mm});
            skCircle(sketch, "E15.1.11.0", {"center": v(28.45, 115.4) * mm, "radius": 1 * mm});
            skCircle(sketch, "E15.1.12.0", {"center": v(28.45, 104.3) * mm, "radius": 1 * mm});
            skCircle(sketch, "E15.1.13.0", {"center": v(28.45, 93.2) * mm, "radius": 1 * mm});
            skCircle(sketch, "E15.1.14.0", {"center": v(28.45, 82.1) * mm, "radius": 1 * mm});
            skCircle(sketch, "E15.1.15.0", {"center": v(28.45, 71) * mm, "radius": 1 * mm});
            skCircle(sketch, "E15.1.16.0", {"center": v(28.45, 59.9) * mm, "radius": 1 * mm});
            skCircle(sketch, "E15.1.17.0", {"center": v(28.45, 48.8) * mm, "radius": 1 * mm});
            skCircle(sketch, "E15.1.18.0", {"center": v(28.45, 37.7) * mm, "radius": 1 * mm});
            skCircle(sketch, "E15.1.19.0", {"center": v(28.45, 26.6) * mm, "radius": 1 * mm});
            skCircle(sketch, "E15.1.20.0", {"center": v(28.45, 15.5) * mm, "radius": 1 * mm});
            skCircle(sketch, "E15.2.0.0", {"center": v(39.4, 237.5) * mm, "radius": 1 * mm});
            skCircle(sketch, "E15.2.1.0", {"center": v(39.4, 226.4) * mm, "radius": 1 * mm});
            skCircle(sketch, "E15.2.2.0", {"center": v(39.4, 215.3) * mm, "radius": 1 * mm});
            skCircle(sketch, "E15.2.3.0", {"center": v(39.4, 204.2) * mm, "radius": 1 * mm});
            skCircle(sketch, "E15.2.4.0", {"center": v(39.4, 193.1) * mm, "radius": 1 * mm});
            skCircle(sketch, "E15.2.5.0", {"center": v(39.4, 182) * mm, "radius": 1 * mm});
            skCircle(sketch, "E15.2.6.0", {"center": v(39.4, 170.9) * mm, "radius": 1 * mm});
            skCircle(sketch, "E15.2.7.0", {"center": v(39.4, 159.8) * mm, "radius": 1 * mm});
            skCircle(sketch, "E15.2.8.0", {"center": v(39.4, 148.7) * mm, "radius": 1 * mm});
            skCircle(sketch, "E15.2.9.0", {"center": v(39.4, 137.6) * mm, "radius": 1 * mm});
            skCircle(sketch, "E15.2.10.0", {"center": v(39.4, 126.5) * mm, "radius": 1 * mm});
            skCircle(sketch, "E15.2.11.0", {"center": v(39.4, 115.4) * mm, "radius": 1 * mm});
            skCircle(sketch, "E15.2.12.0", {"center": v(39.4, 104.3) * mm, "radius": 1 * mm});
            skCircle(sketch, "E15.2.13.0", {"center": v(39.4, 93.2) * mm, "radius": 1 * mm});
            skCircle(sketch, "E15.2.14.0", {"center": v(39.4, 82.1) * mm, "radius": 1 * mm});
            skCircle(sketch, "E15.2.15.0", {"center": v(39.4, 71) * mm, "radius": 1 * mm});
            skCircle(sketch, "E15.2.16.0", {"center": v(39.4, 59.9) * mm, "radius": 1 * mm});
            skCircle(sketch, "E15.2.17.0", {"center": v(39.4, 48.8) * mm, "radius": 1 * mm});
            skCircle(sketch, "E15.2.18.0", {"center": v(39.4, 37.7) * mm, "radius": 1 * mm});
            skCircle(sketch, "E15.2.19.0", {"center": v(39.4, 26.6) * mm, "radius": 1 * mm});
            skCircle(sketch, "E15.2.20.0", {"center": v(39.4, 15.5) * mm, "radius": 1 * mm});
            skCircle(sketch, "E15.3.0.0", {"center": v(50.35, 237.5) * mm, "radius": 1 * mm});
            skCircle(sketch, "E15.3.1.0", {"center": v(50.35, 226.4) * mm, "radius": 1 * mm});
            skCircle(sketch, "E15.3.2.0", {"center": v(50.35, 215.3) * mm, "radius": 1 * mm});
            skCircle(sketch, "E15.3.3.0", {"center": v(50.35, 204.2) * mm, "radius": 1 * mm});
            skCircle(sketch, "E15.3.4.0", {"center": v(50.35, 193.1) * mm, "radius": 1 * mm});
            skCircle(sketch, "E15.3.5.0", {"center": v(50.35, 182) * mm, "radius": 1 * mm});
            skCircle(sketch, "E15.3.6.0", {"center": v(50.35, 170.9) * mm, "radius": 1 * mm});
            skCircle(sketch, "E15.3.7.0", {"center": v(50.35, 159.8) * mm, "radius": 1 * mm});
            skCircle(sketch, "E15.3.8.0", {"center": v(50.35, 148.7) * mm, "radius": 1 * mm});
            skCircle(sketch, "E15.3.9.0", {"center": v(50.35, 137.6) * mm, "radius": 1 * mm});
            skCircle(sketch, "E15.3.10.0", {"center": v(50.35, 126.5) * mm, "radius": 1 * mm});
            skCircle(sketch, "E15.3.11.0", {"center": v(50.35, 115.4) * mm, "radius": 1 * mm});
            skCircle(sketch, "E15.3.12.0", {"center": v(50.35, 104.3) * mm, "radius": 1 * mm});
            skCircle(sketch, "E15.3.13.0", {"center": v(50.35, 93.2) * mm, "radius": 1 * mm});
            skCircle(sketch, "E15.3.14.0", {"center": v(50.35, 82.1) * mm, "radius": 1 * mm});
            skCircle(sketch, "E15.3.15.0", {"center": v(50.35, 71) * mm, "radius": 1 * mm});
            skCircle(sketch, "E15.3.16.0", {"center": v(50.35, 59.9) * mm, "radius": 1 * mm});
            skCircle(sketch, "E15.3.17.0", {"center": v(50.35, 48.8) * mm, "radius": 1 * mm});
            skCircle(sketch, "E15.3.18.0", {"center": v(50.35, 37.7) * mm, "radius": 1 * mm});
            skCircle(sketch, "E15.3.19.0", {"center": v(50.35, 26.6) * mm, "radius": 1 * mm});
            skCircle(sketch, "E15.3.20.0", {"center": v(50.35, 15.5) * mm, "radius": 1 * mm});
            skCircle(sketch, "E15.4.0.0", {"center": v(61.3, 237.5) * mm, "radius": 1 * mm});
            skCircle(sketch, "E15.4.1.0", {"center": v(61.3, 226.4) * mm, "radius": 1 * mm});
            skCircle(sketch, "E15.4.2.0", {"center": v(61.3, 215.3) * mm, "radius": 1 * mm});
            skCircle(sketch, "E15.4.3.0", {"center": v(61.3, 204.2) * mm, "radius": 1 * mm});
            skCircle(sketch, "E15.4.4.0", {"center": v(61.3, 193.1) * mm, "radius": 1 * mm});
            skCircle(sketch, "E15.4.5.0", {"center": v(61.3, 182) * mm, "radius": 1 * mm});
            skCircle(sketch, "E15.4.6.0", {"center": v(61.3, 170.9) * mm, "radius": 1 * mm});
            skCircle(sketch, "E15.4.7.0", {"center": v(61.3, 159.8) * mm, "radius": 1 * mm});
            skCircle(sketch, "E15.4.8.0", {"center": v(61.3, 148.7) * mm, "radius": 1 * mm});
            skCircle(sketch, "E15.4.9.0", {"center": v(61.3, 137.6) * mm, "radius": 1 * mm});
            skCircle(sketch, "E15.4.10.0", {"center": v(61.3, 126.5) * mm, "radius": 1 * mm});
            skCircle(sketch, "E15.4.11.0", {"center": v(61.3, 115.4) * mm, "radius": 1 * mm});
            skCircle(sketch, "E15.4.12.0", {"center": v(61.3, 104.3) * mm, "radius": 1 * mm});
            skCircle(sketch, "E15.4.13.0", {"center": v(61.3, 93.2) * mm, "radius": 1 * mm});
            skCircle(sketch, "E15.4.14.0", {"center": v(61.3, 82.1) * mm, "radius": 1 * mm});
            skCircle(sketch, "E15.4.15.0", {"center": v(61.3, 71) * mm, "radius": 1 * mm});
            skCircle(sketch, "E15.4.16.0", {"center": v(61.3, 59.9) * mm, "radius": 1 * mm});
            skCircle(sketch, "E15.4.17.0", {"center": v(61.3, 48.8) * mm, "radius": 1 * mm});
            skCircle(sketch, "E15.4.18.0", {"center": v(61.3, 37.7) * mm, "radius": 1 * mm});
            skCircle(sketch, "E15.4.19.0", {"center": v(61.3, 26.6) * mm, "radius": 1 * mm});
            skCircle(sketch, "E15.4.20.0", {"center": v(61.3, 15.5) * mm, "radius": 1 * mm});
            skCircle(sketch, "E15.5.0.0", {"center": v(72.25, 237.5) * mm, "radius": 1 * mm});
            skCircle(sketch, "E15.5.1.0", {"center": v(72.25, 226.4) * mm, "radius": 1 * mm});
            skCircle(sketch, "E15.5.2.0", {"center": v(72.25, 215.3) * mm, "radius": 1 * mm});
            skCircle(sketch, "E15.5.3.0", {"center": v(72.25, 204.2) * mm, "radius": 1 * mm});
            skCircle(sketch, "E15.5.4.0", {"center": v(72.25, 193.1) * mm, "radius": 1 * mm});
            skCircle(sketch, "E15.5.5.0", {"center": v(72.25, 182) * mm, "radius": 1 * mm});
            skCircle(sketch, "E15.5.6.0", {"center": v(72.25, 170.9) * mm, "radius": 1 * mm});
            skCircle(sketch, "E15.5.7.0", {"center": v(72.25, 159.8) * mm, "radius": 1 * mm});
            skCircle(sketch, "E15.5.8.0", {"center": v(72.25, 148.7) * mm, "radius": 1 * mm});
            skCircle(sketch, "E15.5.9.0", {"center": v(72.25, 137.6) * mm, "radius": 1 * mm});
            skCircle(sketch, "E15.5.10.0", {"center": v(72.25, 126.5) * mm, "radius": 1 * mm});
            skCircle(sketch, "E15.5.11.0", {"center": v(72.25, 115.4) * mm, "radius": 1 * mm});
            skCircle(sketch, "E15.5.12.0", {"center": v(72.25, 104.3) * mm, "radius": 1 * mm});
            skCircle(sketch, "E15.5.13.0", {"center": v(72.25, 93.2) * mm, "radius": 1 * mm});
            skCircle(sketch, "E15.5.14.0", {"center": v(72.25, 82.1) * mm, "radius": 1 * mm});
            skCircle(sketch, "E15.5.15.0", {"center": v(72.25, 71) * mm, "radius": 1 * mm});
            skCircle(sketch, "E15.5.16.0", {"center": v(72.25, 59.9) * mm, "radius": 1 * mm});
            skCircle(sketch, "E15.5.17.0", {"center": v(72.25, 48.8) * mm, "radius": 1 * mm});
            skCircle(sketch, "E15.5.18.0", {"center": v(72.25, 37.7) * mm, "radius": 1 * mm});
            skCircle(sketch, "E15.5.19.0", {"center": v(72.25, 26.6) * mm, "radius": 1 * mm});
            skCircle(sketch, "E15.5.20.0", {"center": v(72.25, 15.5) * mm, "radius": 1 * mm});
            skCircle(sketch, "E15.6.0.0", {"center": v(83.2, 237.5) * mm, "radius": 1 * mm});
            skCircle(sketch, "E15.6.1.0", {"center": v(83.2, 226.4) * mm, "radius": 1 * mm});
            skCircle(sketch, "E15.6.2.0", {"center": v(83.2, 215.3) * mm, "radius": 1 * mm});
            skCircle(sketch, "E15.6.3.0", {"center": v(83.2, 204.2) * mm, "radius": 1 * mm});
            skCircle(sketch, "E15.6.4.0", {"center": v(83.2, 193.1) * mm, "radius": 1 * mm});
            skCircle(sketch, "E15.6.5.0", {"center": v(83.2, 182) * mm, "radius": 1 * mm});
            skCircle(sketch, "E15.6.6.0", {"center": v(83.2, 170.9) * mm, "radius": 1 * mm});
            skCircle(sketch, "E15.6.7.0", {"center": v(83.2, 159.8) * mm, "radius": 1 * mm});
            skCircle(sketch, "E15.6.8.0", {"center": v(83.2, 148.7) * mm, "radius": 1 * mm});
            skCircle(sketch, "E15.6.9.0", {"center": v(83.2, 137.6) * mm, "radius": 1 * mm});
            skCircle(sketch, "E15.6.10.0", {"center": v(83.2, 126.5) * mm, "radius": 1 * mm});
            skCircle(sketch, "E15.6.11.0", {"center": v(83.2, 115.4) * mm, "radius": 1 * mm});
            skCircle(sketch, "E15.6.12.0", {"center": v(83.2, 104.3) * mm, "radius": 1 * mm});
            skCircle(sketch, "E15.6.13.0", {"center": v(83.2, 93.2) * mm, "radius": 1 * mm});
            skCircle(sketch, "E15.6.14.0", {"center": v(83.2, 82.1) * mm, "radius": 1 * mm});
            skCircle(sketch, "E15.6.15.0", {"center": v(83.2, 71) * mm, "radius": 1 * mm});
            skCircle(sketch, "E15.6.16.0", {"center": v(83.2, 59.9) * mm, "radius": 1 * mm});
            skCircle(sketch, "E15.6.17.0", {"center": v(83.2, 48.8) * mm, "radius": 1 * mm});
            skCircle(sketch, "E15.6.18.0", {"center": v(83.2, 37.7) * mm, "radius": 1 * mm});
            skCircle(sketch, "E15.6.19.0", {"center": v(83.2, 26.6) * mm, "radius": 1 * mm});
            skCircle(sketch, "E15.6.20.0", {"center": v(83.2, 15.5) * mm, "radius": 1 * mm});
            skCircle(sketch, "E15.7.0.0", {"center": v(94.15, 237.5) * mm, "radius": 1 * mm});
            skCircle(sketch, "E15.7.1.0", {"center": v(94.15, 226.4) * mm, "radius": 1 * mm});
            skCircle(sketch, "E15.7.2.0", {"center": v(94.15, 215.3) * mm, "radius": 1 * mm});
            skCircle(sketch, "E15.7.3.0", {"center": v(94.15, 204.2) * mm, "radius": 1 * mm});
            skCircle(sketch, "E15.7.4.0", {"center": v(94.15, 193.1) * mm, "radius": 1 * mm});
            skCircle(sketch, "E15.7.5.0", {"center": v(94.15, 182) * mm, "radius": 1 * mm});
            skCircle(sketch, "E15.7.6.0", {"center": v(94.15, 170.9) * mm, "radius": 1 * mm});
            skCircle(sketch, "E15.7.7.0", {"center": v(94.15, 159.8) * mm, "radius": 1 * mm});
            skCircle(sketch, "E15.7.8.0", {"center": v(94.15, 148.7) * mm, "radius": 1 * mm});
            skCircle(sketch, "E15.7.9.0", {"center": v(94.15, 137.6) * mm, "radius": 1 * mm});
            skCircle(sketch, "E15.7.10.0", {"center": v(94.15, 126.5) * mm, "radius": 1 * mm});
            skCircle(sketch, "E15.7.11.0", {"center": v(94.15, 115.4) * mm, "radius": 1 * mm});
            skCircle(sketch, "E15.7.12.0", {"center": v(94.15, 104.3) * mm, "radius": 1 * mm});
            skCircle(sketch, "E15.7.13.0", {"center": v(94.15, 93.2) * mm, "radius": 1 * mm});
            skCircle(sketch, "E15.7.14.0", {"center": v(94.15, 82.1) * mm, "radius": 1 * mm});
            skCircle(sketch, "E15.7.15.0", {"center": v(94.15, 71) * mm, "radius": 1 * mm});
            skCircle(sketch, "E15.7.16.0", {"center": v(94.15, 59.9) * mm, "radius": 1 * mm});
            skCircle(sketch, "E15.7.17.0", {"center": v(94.15, 48.8) * mm, "radius": 1 * mm});
            skCircle(sketch, "E15.7.18.0", {"center": v(94.15, 37.7) * mm, "radius": 1 * mm});
            skCircle(sketch, "E15.7.19.0", {"center": v(94.15, 26.6) * mm, "radius": 1 * mm});
            skCircle(sketch, "E15.7.20.0", {"center": v(94.15, 15.5) * mm, "radius": 1 * mm});
            skCircle(sketch, "E15.8.0.0", {"center": v(105.1, 237.5) * mm, "radius": 1 * mm});
            skCircle(sketch, "E15.8.1.0", {"center": v(105.1, 226.4) * mm, "radius": 1 * mm});
            skCircle(sketch, "E15.8.2.0", {"center": v(105.1, 215.3) * mm, "radius": 1 * mm});
            skCircle(sketch, "E15.8.3.0", {"center": v(105.1, 204.2) * mm, "radius": 1 * mm});
            skCircle(sketch, "E15.8.4.0", {"center": v(105.1, 193.1) * mm, "radius": 1 * mm});
            skCircle(sketch, "E15.8.5.0", {"center": v(105.1, 182) * mm, "radius": 1 * mm});
            skCircle(sketch, "E15.8.6.0", {"center": v(105.1, 170.9) * mm, "radius": 1 * mm});
            skCircle(sketch, "E15.8.7.0", {"center": v(105.1, 159.8) * mm, "radius": 1 * mm});
            skCircle(sketch, "E15.8.8.0", {"center": v(105.1, 148.7) * mm, "radius": 1 * mm});
            skCircle(sketch, "E15.8.9.0", {"center": v(105.1, 137.6) * mm, "radius": 1 * mm});
            skCircle(sketch, "E15.8.10.0", {"center": v(105.1, 126.5) * mm, "radius": 1 * mm});
            skCircle(sketch, "E15.8.11.0", {"center": v(105.1, 115.4) * mm, "radius": 1 * mm});
            skCircle(sketch, "E15.8.12.0", {"center": v(105.1, 104.3) * mm, "radius": 1 * mm});
            skCircle(sketch, "E15.8.13.0", {"center": v(105.1, 93.2) * mm, "radius": 1 * mm});
            skCircle(sketch, "E15.8.14.0", {"center": v(105.1, 82.1) * mm, "radius": 1 * mm});
            skCircle(sketch, "E15.8.15.0", {"center": v(105.1, 71) * mm, "radius": 1 * mm});
            skCircle(sketch, "E15.8.16.0", {"center": v(105.1, 59.9) * mm, "radius": 1 * mm});
            skCircle(sketch, "E15.8.17.0", {"center": v(105.1, 48.8) * mm, "radius": 1 * mm});
            skCircle(sketch, "E15.8.18.0", {"center": v(105.1, 37.7) * mm, "radius": 1 * mm});
            skCircle(sketch, "E15.8.19.0", {"center": v(105.1, 26.6) * mm, "radius": 1 * mm});
            skCircle(sketch, "E15.8.20.0", {"center": v(105.1, 15.5) * mm, "radius": 1 * mm});
            skCircle(sketch, "E15.9.0.0", {"center": v(116.05, 237.5) * mm, "radius": 1 * mm});
            skCircle(sketch, "E15.9.1.0", {"center": v(116.05, 226.4) * mm, "radius": 1 * mm});
            skCircle(sketch, "E15.9.2.0", {"center": v(116.05, 215.3) * mm, "radius": 1 * mm});
            skCircle(sketch, "E15.9.3.0", {"center": v(116.05, 204.2) * mm, "radius": 1 * mm});
            skCircle(sketch, "E15.9.4.0", {"center": v(116.05, 193.1) * mm, "radius": 1 * mm});
            skCircle(sketch, "E15.9.5.0", {"center": v(116.05, 182) * mm, "radius": 1 * mm});
            skCircle(sketch, "E15.9.6.0", {"center": v(116.05, 170.9) * mm, "radius": 1 * mm});
            skCircle(sketch, "E15.9.7.0", {"center": v(116.05, 159.8) * mm, "radius": 1 * mm});
            skCircle(sketch, "E15.9.8.0", {"center": v(116.05, 148.7) * mm, "radius": 1 * mm});
            skCircle(sketch, "E15.9.9.0", {"center": v(116.05, 137.6) * mm, "radius": 1 * mm});
            skCircle(sketch, "E15.9.10.0", {"center": v(116.05, 126.5) * mm, "radius": 1 * mm});
            skCircle(sketch, "E15.9.11.0", {"center": v(116.05, 115.4) * mm, "radius": 1 * mm});
            skCircle(sketch, "E15.9.12.0", {"center": v(116.05, 104.3) * mm, "radius": 1 * mm});
            skCircle(sketch, "E15.9.13.0", {"center": v(116.05, 93.2) * mm, "radius": 1 * mm});
            skCircle(sketch, "E15.9.14.0", {"center": v(116.05, 82.1) * mm, "radius": 1 * mm});
            skCircle(sketch, "E15.9.15.0", {"center": v(116.05, 71) * mm, "radius": 1 * mm});
            skCircle(sketch, "E15.9.16.0", {"center": v(116.05, 59.9) * mm, "radius": 1 * mm});
            skCircle(sketch, "E15.9.17.0", {"center": v(116.05, 48.8) * mm, "radius": 1 * mm});
            skCircle(sketch, "E15.9.18.0", {"center": v(116.05, 37.7) * mm, "radius": 1 * mm});
            skCircle(sketch, "E15.9.19.0", {"center": v(116.05, 26.6) * mm, "radius": 1 * mm});
            skCircle(sketch, "E15.9.20.0", {"center": v(116.05, 15.5) * mm, "radius": 1 * mm});
            skCircle(sketch, "E15.10.0.0", {"center": v(127, 237.5) * mm, "radius": 1 * mm});
            skCircle(sketch, "E15.10.1.0", {"center": v(127, 226.4) * mm, "radius": 1 * mm});
            skCircle(sketch, "E15.10.2.0", {"center": v(127, 215.3) * mm, "radius": 1 * mm});
            skCircle(sketch, "E15.10.3.0", {"center": v(127, 204.2) * mm, "radius": 1 * mm});
            skCircle(sketch, "E15.10.4.0", {"center": v(127, 193.1) * mm, "radius": 1 * mm});
            skCircle(sketch, "E15.10.5.0", {"center": v(127, 182) * mm, "radius": 1 * mm});
            skCircle(sketch, "E15.10.6.0", {"center": v(127, 170.9) * mm, "radius": 1 * mm});
            skCircle(sketch, "E15.10.7.0", {"center": v(127, 159.8) * mm, "radius": 1 * mm});
            skCircle(sketch, "E15.10.8.0", {"center": v(127, 148.7) * mm, "radius": 1 * mm});
            skCircle(sketch, "E15.10.9.0", {"center": v(127, 137.6) * mm, "radius": 1 * mm});
            skCircle(sketch, "E15.10.10.0", {"center": v(127, 126.5) * mm, "radius": 1 * mm});
            skCircle(sketch, "E15.10.11.0", {"center": v(127, 115.4) * mm, "radius": 1 * mm});
            skCircle(sketch, "E15.10.12.0", {"center": v(127, 104.3) * mm, "radius": 1 * mm});
            skCircle(sketch, "E15.10.13.0", {"center": v(127, 93.2) * mm, "radius": 1 * mm});
            skCircle(sketch, "E15.10.14.0", {"center": v(127, 82.1) * mm, "radius": 1 * mm});
            skCircle(sketch, "E15.10.15.0", {"center": v(127, 71) * mm, "radius": 1 * mm});
            skCircle(sketch, "E15.10.16.0", {"center": v(127, 59.9) * mm, "radius": 1 * mm});
            skCircle(sketch, "E15.10.17.0", {"center": v(127, 48.8) * mm, "radius": 1 * mm});
            skCircle(sketch, "E15.10.18.0", {"center": v(127, 37.7) * mm, "radius": 1 * mm});
            skCircle(sketch, "E15.10.19.0", {"center": v(127, 26.6) * mm, "radius": 1 * mm});
            skCircle(sketch, "E15.10.20.0", {"center": v(127, 15.5) * mm, "radius": 1 * mm});
            skCircle(sketch, "E15.11.0.0", {"center": v(137.95, 237.5) * mm, "radius": 1 * mm});
            skCircle(sketch, "E15.11.1.0", {"center": v(137.95, 226.4) * mm, "radius": 1 * mm});
            skCircle(sketch, "E15.11.2.0", {"center": v(137.95, 215.3) * mm, "radius": 1 * mm});
            skCircle(sketch, "E15.11.3.0", {"center": v(137.95, 204.2) * mm, "radius": 1 * mm});
            skCircle(sketch, "E15.11.4.0", {"center": v(137.95, 193.1) * mm, "radius": 1 * mm});
            skCircle(sketch, "E15.11.5.0", {"center": v(137.95, 182) * mm, "radius": 1 * mm});
            skCircle(sketch, "E15.11.6.0", {"center": v(137.95, 170.9) * mm, "radius": 1 * mm});
            skCircle(sketch, "E15.11.7.0", {"center": v(137.95, 159.8) * mm, "radius": 1 * mm});
            skCircle(sketch, "E15.11.8.0", {"center": v(137.95, 148.7) * mm, "radius": 1 * mm});
            skCircle(sketch, "E15.11.9.0", {"center": v(137.95, 137.6) * mm, "radius": 1 * mm});
            skCircle(sketch, "E15.11.10.0", {"center": v(137.95, 126.5) * mm, "radius": 1 * mm});
            skCircle(sketch, "E15.11.11.0", {"center": v(137.95, 115.4) * mm, "radius": 1 * mm});
            skCircle(sketch, "E15.11.12.0", {"center": v(137.95, 104.3) * mm, "radius": 1 * mm});
            skCircle(sketch, "E15.11.13.0", {"center": v(137.95, 93.2) * mm, "radius": 1 * mm});
            skCircle(sketch, "E15.11.14.0", {"center": v(137.95, 82.1) * mm, "radius": 1 * mm});
            skCircle(sketch, "E15.11.15.0", {"center": v(137.95, 71) * mm, "radius": 1 * mm});
            skCircle(sketch, "E15.11.16.0", {"center": v(137.95, 59.9) * mm, "radius": 1 * mm});
            skCircle(sketch, "E15.11.17.0", {"center": v(137.95, 48.8) * mm, "radius": 1 * mm});
            skCircle(sketch, "E15.11.18.0", {"center": v(137.95, 37.7) * mm, "radius": 1 * mm});
            skCircle(sketch, "E15.11.19.0", {"center": v(137.95, 26.6) * mm, "radius": 1 * mm});
            skCircle(sketch, "E15.11.20.0", {"center": v(137.95, 15.5) * mm, "radius": 1 * mm});
            skCircle(sketch, "E15.12.0.0", {"center": v(148.9, 237.5) * mm, "radius": 1 * mm});
            skCircle(sketch, "E15.12.1.0", {"center": v(148.9, 226.4) * mm, "radius": 1 * mm});
            skCircle(sketch, "E15.12.2.0", {"center": v(148.9, 215.3) * mm, "radius": 1 * mm});
            skCircle(sketch, "E15.12.3.0", {"center": v(148.9, 204.2) * mm, "radius": 1 * mm});
            skCircle(sketch, "E15.12.4.0", {"center": v(148.9, 193.1) * mm, "radius": 1 * mm});
            skCircle(sketch, "E15.12.5.0", {"center": v(148.9, 182) * mm, "radius": 1 * mm});
            skCircle(sketch, "E15.12.6.0", {"center": v(148.9, 170.9) * mm, "radius": 1 * mm});
            skCircle(sketch, "E15.12.7.0", {"center": v(148.9, 159.8) * mm, "radius": 1 * mm});
            skCircle(sketch, "E15.12.8.0", {"center": v(148.9, 148.7) * mm, "radius": 1 * mm});
            skCircle(sketch, "E15.12.9.0", {"center": v(148.9, 137.6) * mm, "radius": 1 * mm});
            skCircle(sketch, "E15.12.10.0", {"center": v(148.9, 126.5) * mm, "radius": 1 * mm});
            skCircle(sketch, "E15.12.11.0", {"center": v(148.9, 115.4) * mm, "radius": 1 * mm});
            skCircle(sketch, "E15.12.12.0", {"center": v(148.9, 104.3) * mm, "radius": 1 * mm});
            skCircle(sketch, "E15.12.13.0", {"center": v(148.9, 93.2) * mm, "radius": 1 * mm});
            skCircle(sketch, "E15.12.14.0", {"center": v(148.9, 82.1) * mm, "radius": 1 * mm});
            skCircle(sketch, "E15.12.15.0", {"center": v(148.9, 71) * mm, "radius": 1 * mm});
            skCircle(sketch, "E15.12.16.0", {"center": v(148.9, 59.9) * mm, "radius": 1 * mm});
            skCircle(sketch, "E15.12.17.0", {"center": v(148.9, 48.8) * mm, "radius": 1 * mm});
            skCircle(sketch, "E15.12.18.0", {"center": v(148.9, 37.7) * mm, "radius": 1 * mm});
            skCircle(sketch, "E15.12.19.0", {"center": v(148.9, 26.6) * mm, "radius": 1 * mm});
            skCircle(sketch, "E15.12.20.0", {"center": v(148.9, 15.5) * mm, "radius": 1 * mm});
            skCircle(sketch, "E15.13.0.0", {"center": v(159.85, 237.5) * mm, "radius": 1 * mm});
            skCircle(sketch, "E15.13.1.0", {"center": v(159.85, 226.4) * mm, "radius": 1 * mm});
            skCircle(sketch, "E15.13.2.0", {"center": v(159.85, 215.3) * mm, "radius": 1 * mm});
            skCircle(sketch, "E15.13.3.0", {"center": v(159.85, 204.2) * mm, "radius": 1 * mm});
            skCircle(sketch, "E15.13.4.0", {"center": v(159.85, 193.1) * mm, "radius": 1 * mm});
            skCircle(sketch, "E15.13.5.0", {"center": v(159.85, 182) * mm, "radius": 1 * mm});
            skCircle(sketch, "E15.13.6.0", {"center": v(159.85, 170.9) * mm, "radius": 1 * mm});
            skCircle(sketch, "E15.13.7.0", {"center": v(159.85, 159.8) * mm, "radius": 1 * mm});
            skCircle(sketch, "E15.13.8.0", {"center": v(159.85, 148.7) * mm, "radius": 1 * mm});
            skCircle(sketch, "E15.13.9.0", {"center": v(159.85, 137.6) * mm, "radius": 1 * mm});
            skCircle(sketch, "E15.13.10.0", {"center": v(159.85, 126.5) * mm, "radius": 1 * mm});
            skCircle(sketch, "E15.13.11.0", {"center": v(159.85, 115.4) * mm, "radius": 1 * mm});
            skCircle(sketch, "E15.13.12.0", {"center": v(159.85, 104.3) * mm, "radius": 1 * mm});
            skCircle(sketch, "E15.13.13.0", {"center": v(159.85, 93.2) * mm, "radius": 1 * mm});
            skCircle(sketch, "E15.13.14.0", {"center": v(159.85, 82.1) * mm, "radius": 1 * mm});
            skCircle(sketch, "E15.13.15.0", {"center": v(159.85, 71) * mm, "radius": 1 * mm});
            skCircle(sketch, "E15.13.16.0", {"center": v(159.85, 59.9) * mm, "radius": 1 * mm});
            skCircle(sketch, "E15.13.17.0", {"center": v(159.85, 48.8) * mm, "radius": 1 * mm});
            skCircle(sketch, "E15.13.18.0", {"center": v(159.85, 37.7) * mm, "radius": 1 * mm});
            skCircle(sketch, "E15.13.19.0", {"center": v(159.85, 26.6) * mm, "radius": 1 * mm});
            skCircle(sketch, "E15.13.20.0", {"center": v(159.85, 15.5) * mm, "radius": 1 * mm});
            skCircle(sketch, "E15.14.0.0", {"center": v(170.8, 237.5) * mm, "radius": 1 * mm});
            skCircle(sketch, "E15.14.1.0", {"center": v(170.8, 226.4) * mm, "radius": 1 * mm});
            skCircle(sketch, "E15.14.2.0", {"center": v(170.8, 215.3) * mm, "radius": 1 * mm});
            skCircle(sketch, "E15.14.3.0", {"center": v(170.8, 204.2) * mm, "radius": 1 * mm});
            skCircle(sketch, "E15.14.4.0", {"center": v(170.8, 193.1) * mm, "radius": 1 * mm});
            skCircle(sketch, "E15.14.5.0", {"center": v(170.8, 182) * mm, "radius": 1 * mm});
            skCircle(sketch, "E15.14.6.0", {"center": v(170.8, 170.9) * mm, "radius": 1 * mm});
            skCircle(sketch, "E15.14.7.0", {"center": v(170.8, 159.8) * mm, "radius": 1 * mm});
            skCircle(sketch, "E15.14.8.0", {"center": v(170.8, 148.7) * mm, "radius": 1 * mm});
            skCircle(sketch, "E15.14.9.0", {"center": v(170.8, 137.6) * mm, "radius": 1 * mm});
            skCircle(sketch, "E15.14.10.0", {"center": v(170.8, 126.5) * mm, "radius": 1 * mm});
            skCircle(sketch, "E15.14.11.0", {"center": v(170.8, 115.4) * mm, "radius": 1 * mm});
            skCircle(sketch, "E15.14.12.0", {"center": v(170.8, 104.3) * mm, "radius": 1 * mm});
            skCircle(sketch, "E15.14.13.0", {"center": v(170.8, 93.2) * mm, "radius": 1 * mm});
            skCircle(sketch, "E15.14.14.0", {"center": v(170.8, 82.1) * mm, "radius": 1 * mm});
            skCircle(sketch, "E15.14.15.0", {"center": v(170.8, 71) * mm, "radius": 1 * mm});
            skCircle(sketch, "E15.14.16.0", {"center": v(170.8, 59.9) * mm, "radius": 1 * mm});
            skCircle(sketch, "E15.14.17.0", {"center": v(170.8, 48.8) * mm, "radius": 1 * mm});
            skCircle(sketch, "E15.14.18.0", {"center": v(170.8, 37.7) * mm, "radius": 1 * mm});
            skCircle(sketch, "E15.14.19.0", {"center": v(170.8, 26.6) * mm, "radius": 1 * mm});
            skCircle(sketch, "E15.14.20.0", {"center": v(170.8, 15.5) * mm, "radius": 1 * mm});
            skCircle(sketch, "E15.15.0.0", {"center": v(181.75, 237.5) * mm, "radius": 1 * mm});
            skCircle(sketch, "E15.15.1.0", {"center": v(181.75, 226.4) * mm, "radius": 1 * mm});
            skCircle(sketch, "E15.15.2.0", {"center": v(181.75, 215.3) * mm, "radius": 1 * mm});
            skCircle(sketch, "E15.15.3.0", {"center": v(181.75, 204.2) * mm, "radius": 1 * mm});
            skCircle(sketch, "E15.15.4.0", {"center": v(181.75, 193.1) * mm, "radius": 1 * mm});
            skCircle(sketch, "E15.15.5.0", {"center": v(181.75, 182) * mm, "radius": 1 * mm});
            skCircle(sketch, "E15.15.6.0", {"center": v(181.75, 170.9) * mm, "radius": 1 * mm});
            skCircle(sketch, "E15.15.7.0", {"center": v(181.75, 159.8) * mm, "radius": 1 * mm});
            skCircle(sketch, "E15.15.8.0", {"center": v(181.75, 148.7) * mm, "radius": 1 * mm});
            skCircle(sketch, "E15.15.9.0", {"center": v(181.75, 137.6) * mm, "radius": 1 * mm});
            skCircle(sketch, "E15.15.10.0", {"center": v(181.75, 126.5) * mm, "radius": 1 * mm});
            skCircle(sketch, "E15.15.11.0", {"center": v(181.75, 115.4) * mm, "radius": 1 * mm});
            skCircle(sketch, "E15.15.12.0", {"center": v(181.75, 104.3) * mm, "radius": 1 * mm});
            skCircle(sketch, "E15.15.13.0", {"center": v(181.75, 93.2) * mm, "radius": 1 * mm});
            skCircle(sketch, "E15.15.14.0", {"center": v(181.75, 82.1) * mm, "radius": 1 * mm});
            skCircle(sketch, "E15.15.15.0", {"center": v(181.75, 71) * mm, "radius": 1 * mm});
            skCircle(sketch, "E15.15.16.0", {"center": v(181.75, 59.9) * mm, "radius": 1 * mm});
            skCircle(sketch, "E15.15.17.0", {"center": v(181.75, 48.8) * mm, "radius": 1 * mm});
            skCircle(sketch, "E15.15.18.0", {"center": v(181.75, 37.7) * mm, "radius": 1 * mm});
            skCircle(sketch, "E15.15.19.0", {"center": v(181.75, 26.6) * mm, "radius": 1 * mm});
            skCircle(sketch, "E15.15.20.0", {"center": v(181.75, 15.5) * mm, "radius": 1 * mm});
            skLineSegment(sketch, "E15.direction1", {"start": v(17.5, 237.5) * mm, "end": v(28.45, 237.5) * mm, "construction": true});
            skLineSegment(sketch, "E15.direction2", {"start": v(17.5, 237.5) * mm, "end": v(17.5, 226.4) * mm, "construction": true});
            skSolve(sketch);
        }
        {
            var Q0;
            Q0=makeQuery(id+"F4.imprint","IMPRINT",FACE,{"disambiguationData":[TD([[makeQuery(id+"F4.imprint","IMPRINT",EDGE,{"derivedFrom":sQuery(id+"F4.wireOp",EDGE,"E12.0.0")}),1.0]])]});
            extrude(context, id + "F5", {"entities" : qUnion([Q0]), "oppositeDirection" : true, "depth" : 3 * mm});
        }
        {
            var Q0;
            Q0=makeQuery(id+"F3.opExtrude","CAP_FACE",FACE,{"disambiguationData":[OSD([sQuery(id+"F2.wireOp",EDGE,"E2.0"),sQuery(id+"F2.wireOp",EDGE,"E3"),sQuery(id+"F2.wireOp",EDGE,"E4"),sQuery(id+"F2.wireOp",EDGE,"E5"),sQuery(id+"F2.wireOp",EDGE,"E7"),sQuery(id+"F2.wireOp",EDGE,"E8.0.1.0"),sQuery(id+"F2.wireOp",EDGE,"E8.0.2.0"),sQuery(id+"F2.wireOp",EDGE,"E8.0.3.0"),sQuery(id+"F2.wireOp",EDGE,"E8.0.4.0"),sQuery(id+"F2.wireOp",EDGE,"E8.0.5.0"),sQuery(id+"F2.wireOp",EDGE,"E8.0.6.0"),sQuery(id+"F2.wireOp",EDGE,"E8.0.7.0"),sQuery(id+"F2.wireOp",EDGE,"E8.0.8.0"),sQuery(id+"F2.wireOp",EDGE,"E8.0.9.0"),sQuery(id+"F2.wireOp",EDGE,"E8.0.10.0"),sQuery(id+"F2.wireOp",EDGE,"E8.0.11.0"),sQuery(id+"F2.wireOp",EDGE,"E8.0.12.0"),sQuery(id+"F2.wireOp",EDGE,"E8.0.13.0"),sQuery(id+"F2.wireOp",EDGE,"E8.0.14.0"),sQuery(id+"F2.wireOp",EDGE,"E8.0.15.0"),sQuery(id+"F2.wireOp",EDGE,"E8.0.16.0"),sQuery(id+"F2.wireOp",EDGE,"E8.0.17.0"),sQuery(id+"F2.wireOp",EDGE,"E8.0.18.0"),sQuery(id+"F2.wireOp",EDGE,"E8.0.19.0"),sQuery(id+"F2.wireOp",EDGE,"E8.1.0.0"),sQuery(id+"F2.wireOp",EDGE,"E8.1.1.0"),sQuery(id+"F2.wireOp",EDGE,"E8.1.2.0"),sQuery(id+"F2.wireOp",EDGE,"E8.1.3.0"),sQuery(id+"F2.wireOp",EDGE,"E8.1.4.0"),sQuery(id+"F2.wireOp",EDGE,"E8.1.5.0"),sQuery(id+"F2.wireOp",EDGE,"E8.1.6.0"),sQuery(id+"F2.wireOp",EDGE,"E8.1.7.0"),sQuery(id+"F2.wireOp",EDGE,"E8.1.8.0"),sQuery(id+"F2.wireOp",EDGE,"E8.1.9.0"),sQuery(id+"F2.wireOp",EDGE,"E8.1.10.0"),sQuery(id+"F2.wireOp",EDGE,"E8.1.11.0"),sQuery(id+"F2.wireOp",EDGE,"E8.1.12.0"),sQuery(id+"F2.wireOp",EDGE,"E8.1.13.0"),sQuery(id+"F2.wireOp",EDGE,"E8.1.14.0"),sQuery(id+"F2.wireOp",EDGE,"E8.1.15.0"),sQuery(id+"F2.wireOp",EDGE,"E8.1.16.0"),sQuery(id+"F2.wireOp",EDGE,"E8.1.17.0"),sQuery(id+"F2.wireOp",EDGE,"E8.1.18.0"),sQuery(id+"F2.wireOp",EDGE,"E8.1.19.0"),sQuery(id+"F2.wireOp",EDGE,"E8.2.0.0"),sQuery(id+"F2.wireOp",EDGE,"E8.2.1.0"),sQuery(id+"F2.wireOp",EDGE,"E8.2.2.0"),sQuery(id+"F2.wireOp",EDGE,"E8.2.3.0"),sQuery(id+"F2.wireOp",EDGE,"E8.2.4.0"),sQuery(id+"F2.wireOp",EDGE,"E8.2.5.0"),sQuery(id+"F2.wireOp",EDGE,"E8.2.6.0"),sQuery(id+"F2.wireOp",EDGE,"E8.2.7.0"),sQuery(id+"F2.wireOp",EDGE,"E8.2.8.0"),sQuery(id+"F2.wireOp",EDGE,"E8.2.9.0"),sQuery(id+"F2.wireOp",EDGE,"E8.2.10.0"),sQuery(id+"F2.wireOp",EDGE,"E8.2.11.0"),sQuery(id+"F2.wireOp",EDGE,"E8.2.12.0"),sQuery(id+"F2.wireOp",EDGE,"E8.2.13.0"),sQuery(id+"F2.wireOp",EDGE,"E8.2.14.0"),sQuery(id+"F2.wireOp",EDGE,"E8.2.15.0"),sQuery(id+"F2.wireOp",EDGE,"E8.2.16.0"),sQuery(id+"F2.wireOp",EDGE,"E8.2.17.0"),sQuery(id+"F2.wireOp",EDGE,"E8.2.18.0"),sQuery(id+"F2.wireOp",EDGE,"E8.2.19.0"),sQuery(id+"F2.wireOp",EDGE,"E8.3.0.0"),sQuery(id+"F2.wireOp",EDGE,"E8.3.1.0"),sQuery(id+"F2.wireOp",EDGE,"E8.3.2.0"),sQuery(id+"F2.wireOp",EDGE,"E8.3.3.0"),sQuery(id+"F2.wireOp",EDGE,"E8.3.4.0"),sQuery(id+"F2.wireOp",EDGE,"E8.3.5.0"),sQuery(id+"F2.wireOp",EDGE,"E8.3.6.0"),sQuery(id+"F2.wireOp",EDGE,"E8.3.7.0"),sQuery(id+"F2.wireOp",EDGE,"E8.3.8.0"),sQuery(id+"F2.wireOp",EDGE,"E8.3.9.0"),sQuery(id+"F2.wireOp",EDGE,"E8.3.10.0"),sQuery(id+"F2.wireOp",EDGE,"E8.3.11.0"),sQuery(id+"F2.wireOp",EDGE,"E8.3.12.0"),sQuery(id+"F2.wireOp",EDGE,"E8.3.13.0"),sQuery(id+"F2.wireOp",EDGE,"E8.3.14.0"),sQuery(id+"F2.wireOp",EDGE,"E8.3.15.0"),sQuery(id+"F2.wireOp",EDGE,"E8.3.16.0"),sQuery(id+"F2.wireOp",EDGE,"E8.3.17.0"),sQuery(id+"F2.wireOp",EDGE,"E8.3.18.0"),sQuery(id+"F2.wireOp",EDGE,"E8.3.19.0"),sQuery(id+"F2.wireOp",EDGE,"E8.4.0.0"),sQuery(id+"F2.wireOp",EDGE,"E8.4.1.0"),sQuery(id+"F2.wireOp",EDGE,"E8.4.2.0"),sQuery(id+"F2.wireOp",EDGE,"E8.4.3.0"),sQuery(id+"F2.wireOp",EDGE,"E8.4.4.0"),sQuery(id+"F2.wireOp",EDGE,"E8.4.5.0"),sQuery(id+"F2.wireOp",EDGE,"E8.4.6.0"),sQuery(id+"F2.wireOp",EDGE,"E8.4.7.0"),sQuery(id+"F2.wireOp",EDGE,"E8.4.8.0"),sQuery(id+"F2.wireOp",EDGE,"E8.4.9.0"),sQuery(id+"F2.wireOp",EDGE,"E8.4.10.0"),sQuery(id+"F2.wireOp",EDGE,"E8.4.11.0"),sQuery(id+"F2.wireOp",EDGE,"E8.4.12.0"),sQuery(id+"F2.wireOp",EDGE,"E8.4.13.0"),sQuery(id+"F2.wireOp",EDGE,"E8.4.14.0"),sQuery(id+"F2.wireOp",EDGE,"E8.4.15.0"),sQuery(id+"F2.wireOp",EDGE,"E8.4.16.0"),sQuery(id+"F2.wireOp",EDGE,"E8.4.17.0"),sQuery(id+"F2.wireOp",EDGE,"E8.4.18.0"),sQuery(id+"F2.wireOp",EDGE,"E8.4.19.0"),sQuery(id+"F2.wireOp",EDGE,"E8.5.0.0"),sQuery(id+"F2.wireOp",EDGE,"E8.5.1.0"),sQuery(id+"F2.wireOp",EDGE,"E8.5.2.0"),sQuery(id+"F2.wireOp",EDGE,"E8.5.3.0"),sQuery(id+"F2.wireOp",EDGE,"E8.5.4.0"),sQuery(id+"F2.wireOp",EDGE,"E8.5.5.0"),sQuery(id+"F2.wireOp",EDGE,"E8.5.6.0"),sQuery(id+"F2.wireOp",EDGE,"E8.5.7.0"),sQuery(id+"F2.wireOp",EDGE,"E8.5.8.0"),sQuery(id+"F2.wireOp",EDGE,"E8.5.9.0"),sQuery(id+"F2.wireOp",EDGE,"E8.5.10.0"),sQuery(id+"F2.wireOp",EDGE,"E8.5.11.0"),sQuery(id+"F2.wireOp",EDGE,"E8.5.12.0"),sQuery(id+"F2.wireOp",EDGE,"E8.5.13.0"),sQuery(id+"F2.wireOp",EDGE,"E8.5.14.0"),sQuery(id+"F2.wireOp",EDGE,"E8.5.15.0"),sQuery(id+"F2.wireOp",EDGE,"E8.5.16.0"),sQuery(id+"F2.wireOp",EDGE,"E8.5.17.0"),sQuery(id+"F2.wireOp",EDGE,"E8.5.18.0"),sQuery(id+"F2.wireOp",EDGE,"E8.5.19.0"),sQuery(id+"F2.wireOp",EDGE,"E8.6.0.0"),sQuery(id+"F2.wireOp",EDGE,"E8.6.1.0"),sQuery(id+"F2.wireOp",EDGE,"E8.6.2.0"),sQuery(id+"F2.wireOp",EDGE,"E8.6.3.0"),sQuery(id+"F2.wireOp",EDGE,"E8.6.4.0"),sQuery(id+"F2.wireOp",EDGE,"E8.6.5.0"),sQuery(id+"F2.wireOp",EDGE,"E8.6.6.0"),sQuery(id+"F2.wireOp",EDGE,"E8.6.7.0"),sQuery(id+"F2.wireOp",EDGE,"E8.6.8.0"),sQuery(id+"F2.wireOp",EDGE,"E8.6.9.0"),sQuery(id+"F2.wireOp",EDGE,"E8.6.10.0"),sQuery(id+"F2.wireOp",EDGE,"E8.6.11.0"),sQuery(id+"F2.wireOp",EDGE,"E8.6.12.0"),sQuery(id+"F2.wireOp",EDGE,"E8.6.13.0"),sQuery(id+"F2.wireOp",EDGE,"E8.6.14.0"),sQuery(id+"F2.wireOp",EDGE,"E8.6.15.0"),sQuery(id+"F2.wireOp",EDGE,"E8.6.16.0"),sQuery(id+"F2.wireOp",EDGE,"E8.6.17.0"),sQuery(id+"F2.wireOp",EDGE,"E8.6.18.0"),sQuery(id+"F2.wireOp",EDGE,"E8.6.19.0"),sQuery(id+"F2.wireOp",EDGE,"E8.7.0.0"),sQuery(id+"F2.wireOp",EDGE,"E8.7.1.0"),sQuery(id+"F2.wireOp",EDGE,"E8.7.2.0"),sQuery(id+"F2.wireOp",EDGE,"E8.7.3.0"),sQuery(id+"F2.wireOp",EDGE,"E8.7.4.0"),sQuery(id+"F2.wireOp",EDGE,"E8.7.5.0"),sQuery(id+"F2.wireOp",EDGE,"E8.7.6.0"),sQuery(id+"F2.wireOp",EDGE,"E8.7.7.0"),sQuery(id+"F2.wireOp",EDGE,"E8.7.8.0"),sQuery(id+"F2.wireOp",EDGE,"E8.7.9.0"),sQuery(id+"F2.wireOp",EDGE,"E8.7.10.0"),sQuery(id+"F2.wireOp",EDGE,"E8.7.11.0"),sQuery(id+"F2.wireOp",EDGE,"E8.7.12.0"),sQuery(id+"F2.wireOp",EDGE,"E8.7.13.0"),sQuery(id+"F2.wireOp",EDGE,"E8.7.14.0"),sQuery(id+"F2.wireOp",EDGE,"E8.7.15.0"),sQuery(id+"F2.wireOp",EDGE,"E8.7.16.0"),sQuery(id+"F2.wireOp",EDGE,"E8.7.17.0"),sQuery(id+"F2.wireOp",EDGE,"E8.7.18.0"),sQuery(id+"F2.wireOp",EDGE,"E8.7.19.0"),sQuery(id+"F2.wireOp",EDGE,"E8.8.0.0"),sQuery(id+"F2.wireOp",EDGE,"E8.8.1.0"),sQuery(id+"F2.wireOp",EDGE,"E8.8.2.0"),sQuery(id+"F2.wireOp",EDGE,"E8.8.3.0"),sQuery(id+"F2.wireOp",EDGE,"E8.8.4.0"),sQuery(id+"F2.wireOp",EDGE,"E8.8.5.0"),sQuery(id+"F2.wireOp",EDGE,"E8.8.6.0"),sQuery(id+"F2.wireOp",EDGE,"E8.8.7.0"),sQuery(id+"F2.wireOp",EDGE,"E8.8.8.0"),sQuery(id+"F2.wireOp",EDGE,"E8.8.9.0"),sQuery(id+"F2.wireOp",EDGE,"E8.8.10.0"),sQuery(id+"F2.wireOp",EDGE,"E8.8.11.0"),sQuery(id+"F2.wireOp",EDGE,"E8.8.12.0"),sQuery(id+"F2.wireOp",EDGE,"E8.8.13.0"),sQuery(id+"F2.wireOp",EDGE,"E8.8.14.0"),sQuery(id+"F2.wireOp",EDGE,"E8.8.15.0"),sQuery(id+"F2.wireOp",EDGE,"E8.8.16.0"),sQuery(id+"F2.wireOp",EDGE,"E8.8.17.0"),sQuery(id+"F2.wireOp",EDGE,"E8.8.18.0"),sQuery(id+"F2.wireOp",EDGE,"E8.8.19.0"),sQuery(id+"F2.wireOp",EDGE,"E8.9.0.0"),sQuery(id+"F2.wireOp",EDGE,"E8.9.1.0"),sQuery(id+"F2.wireOp",EDGE,"E8.9.2.0"),sQuery(id+"F2.wireOp",EDGE,"E8.9.3.0"),sQuery(id+"F2.wireOp",EDGE,"E8.9.4.0"),sQuery(id+"F2.wireOp",EDGE,"E8.9.5.0"),sQuery(id+"F2.wireOp",EDGE,"E8.9.6.0"),sQuery(id+"F2.wireOp",EDGE,"E8.9.7.0"),sQuery(id+"F2.wireOp",EDGE,"E8.9.8.0"),sQuery(id+"F2.wireOp",EDGE,"E8.9.9.0"),sQuery(id+"F2.wireOp",EDGE,"E8.9.10.0"),sQuery(id+"F2.wireOp",EDGE,"E8.9.11.0"),sQuery(id+"F2.wireOp",EDGE,"E8.9.12.0"),sQuery(id+"F2.wireOp",EDGE,"E8.9.13.0"),sQuery(id+"F2.wireOp",EDGE,"E8.9.14.0"),sQuery(id+"F2.wireOp",EDGE,"E8.9.15.0"),sQuery(id+"F2.wireOp",EDGE,"E8.9.16.0"),sQuery(id+"F2.wireOp",EDGE,"E8.9.17.0"),sQuery(id+"F2.wireOp",EDGE,"E8.9.18.0"),sQuery(id+"F2.wireOp",EDGE,"E8.9.19.0"),sQuery(id+"F2.wireOp",EDGE,"E8.10.0.0"),sQuery(id+"F2.wireOp",EDGE,"E8.10.1.0"),sQuery(id+"F2.wireOp",EDGE,"E8.10.2.0"),sQuery(id+"F2.wireOp",EDGE,"E8.10.3.0"),sQuery(id+"F2.wireOp",EDGE,"E8.10.4.0"),sQuery(id+"F2.wireOp",EDGE,"E8.10.5.0"),sQuery(id+"F2.wireOp",EDGE,"E8.10.6.0"),sQuery(id+"F2.wireOp",EDGE,"E8.10.7.0"),sQuery(id+"F2.wireOp",EDGE,"E8.10.8.0"),sQuery(id+"F2.wireOp",EDGE,"E8.10.9.0"),sQuery(id+"F2.wireOp",EDGE,"E8.10.10.0"),sQuery(id+"F2.wireOp",EDGE,"E8.10.11.0"),sQuery(id+"F2.wireOp",EDGE,"E8.10.12.0"),sQuery(id+"F2.wireOp",EDGE,"E8.10.13.0"),sQuery(id+"F2.wireOp",EDGE,"E8.10.14.0"),sQuery(id+"F2.wireOp",EDGE,"E8.10.15.0"),sQuery(id+"F2.wireOp",EDGE,"E8.10.16.0"),sQuery(id+"F2.wireOp",EDGE,"E8.10.17.0"),sQuery(id+"F2.wireOp",EDGE,"E8.10.18.0"),sQuery(id+"F2.wireOp",EDGE,"E8.10.19.0"),sQuery(id+"F2.wireOp",EDGE,"E8.11.0.0"),sQuery(id+"F2.wireOp",EDGE,"E8.11.1.0"),sQuery(id+"F2.wireOp",EDGE,"E8.11.2.0"),sQuery(id+"F2.wireOp",EDGE,"E8.11.3.0"),sQuery(id+"F2.wireOp",EDGE,"E8.11.4.0"),sQuery(id+"F2.wireOp",EDGE,"E8.11.5.0"),sQuery(id+"F2.wireOp",EDGE,"E8.11.6.0"),sQuery(id+"F2.wireOp",EDGE,"E8.11.7.0"),sQuery(id+"F2.wireOp",EDGE,"E8.11.8.0"),sQuery(id+"F2.wireOp",EDGE,"E8.11.9.0"),sQuery(id+"F2.wireOp",EDGE,"E8.11.10.0"),sQuery(id+"F2.wireOp",EDGE,"E8.11.11.0"),sQuery(id+"F2.wireOp",EDGE,"E8.11.12.0"),sQuery(id+"F2.wireOp",EDGE,"E8.11.13.0"),sQuery(id+"F2.wireOp",EDGE,"E8.11.14.0"),sQuery(id+"F2.wireOp",EDGE,"E8.11.15.0"),sQuery(id+"F2.wireOp",EDGE,"E8.11.16.0"),sQuery(id+"F2.wireOp",EDGE,"E8.11.17.0"),sQuery(id+"F2.wireOp",EDGE,"E8.11.18.0"),sQuery(id+"F2.wireOp",EDGE,"E8.11.19.0"),sQuery(id+"F2.wireOp",EDGE,"E8.12.0.0"),sQuery(id+"F2.wireOp",EDGE,"E8.12.1.0"),sQuery(id+"F2.wireOp",EDGE,"E8.12.2.0"),sQuery(id+"F2.wireOp",EDGE,"E8.12.3.0"),sQuery(id+"F2.wireOp",EDGE,"E8.12.4.0"),sQuery(id+"F2.wireOp",EDGE,"E8.12.5.0"),sQuery(id+"F2.wireOp",EDGE,"E8.12.6.0"),sQuery(id+"F2.wireOp",EDGE,"E8.12.7.0"),sQuery(id+"F2.wireOp",EDGE,"E8.12.8.0"),sQuery(id+"F2.wireOp",EDGE,"E8.12.9.0"),sQuery(id+"F2.wireOp",EDGE,"E8.12.10.0"),sQuery(id+"F2.wireOp",EDGE,"E8.12.11.0"),sQuery(id+"F2.wireOp",EDGE,"E8.12.12.0"),sQuery(id+"F2.wireOp",EDGE,"E8.12.13.0"),sQuery(id+"F2.wireOp",EDGE,"E8.12.14.0"),sQuery(id+"F2.wireOp",EDGE,"E8.12.15.0"),sQuery(id+"F2.wireOp",EDGE,"E8.12.16.0"),sQuery(id+"F2.wireOp",EDGE,"E8.12.17.0"),sQuery(id+"F2.wireOp",EDGE,"E8.12.18.0"),sQuery(id+"F2.wireOp",EDGE,"E8.12.19.0"),sQuery(id+"F2.wireOp",EDGE,"E8.13.0.0"),sQuery(id+"F2.wireOp",EDGE,"E8.13.1.0"),sQuery(id+"F2.wireOp",EDGE,"E8.13.2.0"),sQuery(id+"F2.wireOp",EDGE,"E8.13.3.0"),sQuery(id+"F2.wireOp",EDGE,"E8.13.4.0"),sQuery(id+"F2.wireOp",EDGE,"E8.13.5.0"),sQuery(id+"F2.wireOp",EDGE,"E8.13.6.0"),sQuery(id+"F2.wireOp",EDGE,"E8.13.7.0"),sQuery(id+"F2.wireOp",EDGE,"E8.13.8.0"),sQuery(id+"F2.wireOp",EDGE,"E8.13.9.0"),sQuery(id+"F2.wireOp",EDGE,"E8.13.10.0"),sQuery(id+"F2.wireOp",EDGE,"E8.13.11.0"),sQuery(id+"F2.wireOp",EDGE,"E8.13.12.0"),sQuery(id+"F2.wireOp",EDGE,"E8.13.13.0"),sQuery(id+"F2.wireOp",EDGE,"E8.13.14.0"),sQuery(id+"F2.wireOp",EDGE,"E8.13.15.0"),sQuery(id+"F2.wireOp",EDGE,"E8.13.16.0"),sQuery(id+"F2.wireOp",EDGE,"E8.13.17.0"),sQuery(id+"F2.wireOp",EDGE,"E8.13.18.0"),sQuery(id+"F2.wireOp",EDGE,"E8.13.19.0"),sQuery(id+"F2.wireOp",EDGE,"E8.14.0.0"),sQuery(id+"F2.wireOp",EDGE,"E8.14.1.0"),sQuery(id+"F2.wireOp",EDGE,"E8.14.2.0"),sQuery(id+"F2.wireOp",EDGE,"E8.14.3.0"),sQuery(id+"F2.wireOp",EDGE,"E8.14.4.0"),sQuery(id+"F2.wireOp",EDGE,"E8.14.5.0"),sQuery(id+"F2.wireOp",EDGE,"E8.14.6.0"),sQuery(id+"F2.wireOp",EDGE,"E8.14.7.0"),sQuery(id+"F2.wireOp",EDGE,"E8.14.8.0"),sQuery(id+"F2.wireOp",EDGE,"E8.14.9.0"),sQuery(id+"F2.wireOp",EDGE,"E8.14.10.0"),sQuery(id+"F2.wireOp",EDGE,"E8.14.11.0"),sQuery(id+"F2.wireOp",EDGE,"E8.14.12.0"),sQuery(id+"F2.wireOp",EDGE,"E8.14.13.0"),sQuery(id+"F2.wireOp",EDGE,"E8.14.14.0"),sQuery(id+"F2.wireOp",EDGE,"E8.14.15.0"),sQuery(id+"F2.wireOp",EDGE,"E8.14.16.0"),sQuery(id+"F2.wireOp",EDGE,"E8.14.17.0"),sQuery(id+"F2.wireOp",EDGE,"E8.14.18.0"),sQuery(id+"F2.wireOp",EDGE,"E8.14.19.0"),sQuery(id+"F2.wireOp",EDGE,"E9.0.15.0"),sQuery(id+"F2.wireOp",EDGE,"E9.0.15.1"),sQuery(id+"F2.wireOp",EDGE,"E9.0.15.2"),sQuery(id+"F2.wireOp",EDGE,"E9.0.15.3"),sQuery(id+"F2.wireOp",EDGE,"E9.0.15.4"),sQuery(id+"F2.wireOp",EDGE,"E9.0.15.5"),sQuery(id+"F2.wireOp",EDGE,"E9.0.15.6"),sQuery(id+"F2.wireOp",EDGE,"E9.0.15.7"),sQuery(id+"F2.wireOp",EDGE,"E9.0.15.8"),sQuery(id+"F2.wireOp",EDGE,"E9.0.15.9"),sQuery(id+"F2.wireOp",EDGE,"E9.0.15.10"),sQuery(id+"F2.wireOp",EDGE,"E9.0.15.11"),sQuery(id+"F2.wireOp",EDGE,"E9.0.15.12"),sQuery(id+"F2.wireOp",EDGE,"E9.0.15.13"),sQuery(id+"F2.wireOp",EDGE,"E9.0.15.14"),sQuery(id+"F2.wireOp",EDGE,"E9.0.15.15"),sQuery(id+"F2.wireOp",EDGE,"E9.0.15.16"),sQuery(id+"F2.wireOp",EDGE,"E9.0.15.17"),sQuery(id+"F2.wireOp",EDGE,"E9.0.15.18"),sQuery(id+"F2.wireOp",EDGE,"E9.0.15.19"),sQuery(id+"F2.wireOp",EDGE,"E10.0.0.20"),sQuery(id+"F2.wireOp",EDGE,"E10.0.1.20"),sQuery(id+"F2.wireOp",EDGE,"E10.0.2.20"),sQuery(id+"F2.wireOp",EDGE,"E10.0.3.20"),sQuery(id+"F2.wireOp",EDGE,"E10.0.4.20"),sQuery(id+"F2.wireOp",EDGE,"E10.0.5.20"),sQuery(id+"F2.wireOp",EDGE,"E10.0.6.20"),sQuery(id+"F2.wireOp",EDGE,"E10.0.7.20"),sQuery(id+"F2.wireOp",EDGE,"E10.0.8.20"),sQuery(id+"F2.wireOp",EDGE,"E10.0.9.20"),sQuery(id+"F2.wireOp",EDGE,"E10.0.10.20"),sQuery(id+"F2.wireOp",EDGE,"E10.0.11.20"),sQuery(id+"F2.wireOp",EDGE,"E10.0.12.20"),sQuery(id+"F2.wireOp",EDGE,"E10.0.13.20"),sQuery(id+"F2.wireOp",EDGE,"E10.0.14.20"),sQuery(id+"F2.wireOp",EDGE,"E10.0.15.20"),sQuery(id+"F2.wireOp",EDGE,"E11")])],"isStart":false});
            var sketch = newSketch(context, id + "F6", { "sketchPlane" : qUnion([Q0])});
            skLineSegment(sketch, "E16.0", {"start": v(-10, 65) * mm, "end": v(-10, -260) * mm});
            skLineSegment(sketch, "E17.0", {"start": v(210, 65) * mm, "end": v(-10, 65) * mm});
            skLineSegment(sketch, "E18.0", {"start": v(210, -260) * mm, "end": v(210, 65) * mm});
            skLineSegment(sketch, "E19.0", {"start": v(-10, -260) * mm, "end": v(210, -260) * mm});
            skLineSegment(sketch, "E20.0", {"start": v(185, 55) * mm, "end": v(15, 55) * mm});
            skLineSegment(sketch, "E21.0", {"start": v(15, -10) * mm, "end": v(185, -10) * mm, "construction": true});
            skLineSegment(sketch, "E22.0", {"start": v(15, -240) * mm, "end": v(15, -10) * mm, "construction": true});
            skLineSegment(sketch, "E23.0", {"start": v(15, -240) * mm, "end": v(185, -240) * mm, "construction": true});
            skLineSegment(sketch, "E24.0", {"start": v(185, -240) * mm, "end": v(185, -10) * mm, "construction": true});
            skLineSegment(sketch, "E25", {"start": v(15, -240) * mm, "end": v(15, 55) * mm});
            skLineSegment(sketch, "E26", {"start": v(15, -240) * mm, "end": v(185, -240) * mm});
            skLineSegment(sketch, "E27", {"start": v(185, 55) * mm, "end": v(185, -240) * mm});
            skLineSegment(sketch, "E28.bottom", {"start": v(15, -29.4) * mm, "end": v(85.7, -29.4) * mm});
            skLineSegment(sketch, "E28.top", {"start": v(15, -34.9) * mm, "end": v(85.7, -34.9) * mm});
            skLineSegment(sketch, "E28.left", {"start": v(15, -29.4) * mm, "end": v(15, -34.9) * mm});
            skLineSegment(sketch, "E28.right", {"start": v(85.7, -29.4) * mm, "end": v(85.7, -34.9) * mm});
            skLineSegment(sketch, "E29.0.1.0", {"start": v(15, -51.6) * mm, "end": v(85.7, -51.6) * mm});
            skLineSegment(sketch, "E29.0.1.1", {"start": v(15, -57.1) * mm, "end": v(85.7, -57.1) * mm});
            skLineSegment(sketch, "E29.0.1.2", {"start": v(85.7, -51.6) * mm, "end": v(85.7, -57.1) * mm});
            skLineSegment(sketch, "E29.0.2.0", {"start": v(15, -73.8) * mm, "end": v(85.7, -73.8) * mm});
            skLineSegment(sketch, "E29.0.2.1", {"start": v(15, -79.3) * mm, "end": v(85.7, -79.3) * mm});
            skLineSegment(sketch, "E29.0.2.2", {"start": v(85.7, -73.8) * mm, "end": v(85.7, -79.3) * mm});
            skLineSegment(sketch, "E29.0.3.0", {"start": v(15, -96) * mm, "end": v(85.7, -96) * mm});
            skLineSegment(sketch, "E29.0.3.1", {"start": v(15, -101.5) * mm, "end": v(85.7, -101.5) * mm});
            skLineSegment(sketch, "E29.0.3.2", {"start": v(85.7, -96) * mm, "end": v(85.7, -101.5) * mm});
            skLineSegment(sketch, "E29.0.4.0", {"start": v(15, -118.2) * mm, "end": v(85.7, -118.2) * mm});
            skLineSegment(sketch, "E29.0.4.1", {"start": v(15, -123.7) * mm, "end": v(85.7, -123.7) * mm});
            skLineSegment(sketch, "E29.0.4.2", {"start": v(85.7, -118.2) * mm, "end": v(85.7, -123.7) * mm});
            skLineSegment(sketch, "E29.0.5.0", {"start": v(15, -140.4) * mm, "end": v(85.7, -140.4) * mm});
            skLineSegment(sketch, "E29.0.5.1", {"start": v(15, -145.9) * mm, "end": v(85.7, -145.9) * mm});
            skLineSegment(sketch, "E29.0.5.2", {"start": v(85.7, -140.4) * mm, "end": v(85.7, -145.9) * mm});
            skLineSegment(sketch, "E29.0.6.0", {"start": v(15, -162.6) * mm, "end": v(85.7, -162.6) * mm});
            skLineSegment(sketch, "E29.0.6.1", {"start": v(15, -168.1) * mm, "end": v(85.7, -168.1) * mm});
            skLineSegment(sketch, "E29.0.6.2", {"start": v(85.7, -162.6) * mm, "end": v(85.7, -168.1) * mm});
            skLineSegment(sketch, "E29.0.7.0", {"start": v(15, -184.8) * mm, "end": v(85.7, -184.8) * mm});
            skLineSegment(sketch, "E29.0.7.1", {"start": v(15, -190.3) * mm, "end": v(85.7, -190.3) * mm});
            skLineSegment(sketch, "E29.0.7.2", {"start": v(85.7, -184.8) * mm, "end": v(85.7, -190.3) * mm});
            skLineSegment(sketch, "E29.1.0.0", {"start": v(114.3, -29.4) * mm, "end": v(185, -29.4) * mm});
            skLineSegment(sketch, "E29.1.0.1", {"start": v(114.3, -34.9) * mm, "end": v(185, -34.9) * mm});
            skLineSegment(sketch, "E29.1.0.2", {"start": v(185, -29.4) * mm, "end": v(185, -34.9) * mm});
            skLineSegment(sketch, "E29.1.1.0", {"start": v(114.3, -51.6) * mm, "end": v(185, -51.6) * mm});
            skLineSegment(sketch, "E29.1.1.1", {"start": v(114.3, -57.1) * mm, "end": v(185, -57.1) * mm});
            skLineSegment(sketch, "E29.1.1.2", {"start": v(185, -51.6) * mm, "end": v(185, -57.1) * mm});
            skLineSegment(sketch, "E29.1.2.0", {"start": v(114.3, -73.8) * mm, "end": v(185, -73.8) * mm});
            skLineSegment(sketch, "E29.1.2.1", {"start": v(114.3, -79.3) * mm, "end": v(185, -79.3) * mm});
            skLineSegment(sketch, "E29.1.2.2", {"start": v(185, -73.8) * mm, "end": v(185, -79.3) * mm});
            skLineSegment(sketch, "E29.1.3.0", {"start": v(114.3, -96) * mm, "end": v(185, -96) * mm});
            skLineSegment(sketch, "E29.1.3.1", {"start": v(114.3, -101.5) * mm, "end": v(185, -101.5) * mm});
            skLineSegment(sketch, "E29.1.3.2", {"start": v(185, -96) * mm, "end": v(185, -101.5) * mm});
            skLineSegment(sketch, "E29.1.4.0", {"start": v(114.3, -118.2) * mm, "end": v(185, -118.2) * mm});
            skLineSegment(sketch, "E29.1.4.1", {"start": v(114.3, -123.7) * mm, "end": v(185, -123.7) * mm});
            skLineSegment(sketch, "E29.1.4.2", {"start": v(185, -118.2) * mm, "end": v(185, -123.7) * mm});
            skLineSegment(sketch, "E29.1.5.0", {"start": v(114.3, -140.4) * mm, "end": v(185, -140.4) * mm});
            skLineSegment(sketch, "E29.1.5.1", {"start": v(114.3, -145.9) * mm, "end": v(185, -145.9) * mm});
            skLineSegment(sketch, "E29.1.5.2", {"start": v(185, -140.4) * mm, "end": v(185, -145.9) * mm});
            skLineSegment(sketch, "E29.1.6.0", {"start": v(114.3, -162.6) * mm, "end": v(185, -162.6) * mm});
            skLineSegment(sketch, "E29.1.6.1", {"start": v(114.3, -168.1) * mm, "end": v(185, -168.1) * mm});
            skLineSegment(sketch, "E29.1.6.2", {"start": v(185, -162.6) * mm, "end": v(185, -168.1) * mm});
            skLineSegment(sketch, "E29.1.7.0", {"start": v(114.3, -184.8) * mm, "end": v(185, -184.8) * mm});
            skLineSegment(sketch, "E29.1.7.1", {"start": v(114.3, -190.3) * mm, "end": v(185, -190.3) * mm});
            skLineSegment(sketch, "E29.1.7.2", {"start": v(185, -184.8) * mm, "end": v(185, -190.3) * mm});
            skLineSegment(sketch, "E29.direction1", {"start": v(15, -29.4) * mm, "end": v(114.3, -29.4) * mm, "construction": true});
            skLineSegment(sketch, "E29.direction2", {"start": v(15, -29.4) * mm, "end": v(15, -51.6) * mm, "construction": true});
            skLineSegment(sketch, "E30.0.1.0", {"start": v(15, -223.6) * mm, "end": v(85.7, -223.6) * mm});
            skLineSegment(sketch, "E30.0.1.1", {"start": v(15, -218.1) * mm, "end": v(85.7, -218.1) * mm});
            skLineSegment(sketch, "E30.0.1.2", {"start": v(85.7, -218.1) * mm, "end": v(85.7, -223.6) * mm});
            skLineSegment(sketch, "E30.0.1.3", {"start": v(114.3, -218.1) * mm, "end": v(185, -218.1) * mm});
            skLineSegment(sketch, "E30.0.1.4", {"start": v(114.3, -223.6) * mm, "end": v(185, -223.6) * mm});
            skLineSegment(sketch, "E30.direction1", {"start": v(15, -190.3) * mm, "end": v(40, -190.3) * mm, "construction": true});
            skLineSegment(sketch, "E30.direction2", {"start": v(15, -190.3) * mm, "end": v(15, -223.6) * mm, "construction": true});
            skLineSegment(sketch, "E31", {"start": v(114.3, -29.4) * mm, "end": v(114.3, -34.9) * mm});
            skLineSegment(sketch, "E32", {"start": v(114.3, -51.6) * mm, "end": v(114.3, -57.1) * mm});
            skLineSegment(sketch, "E33", {"start": v(114.3, -73.8) * mm, "end": v(114.3, -79.3) * mm});
            skLineSegment(sketch, "E34", {"start": v(114.3, -96) * mm, "end": v(114.3, -101.5) * mm});
            skLineSegment(sketch, "E35", {"start": v(114.3, -118.2) * mm, "end": v(114.3, -123.7) * mm});
            skLineSegment(sketch, "E36", {"start": v(114.3, -140.4) * mm, "end": v(114.3, -145.9) * mm});
            skLineSegment(sketch, "E37", {"start": v(114.3, -162.6) * mm, "end": v(114.3, -168.1) * mm});
            skLineSegment(sketch, "E38", {"start": v(114.3, -184.8) * mm, "end": v(114.3, -190.3) * mm});
            skLineSegment(sketch, "E39", {"start": v(114.3, -218.1) * mm, "end": v(114.3, -223.6) * mm});
            skLineSegment(sketch, "E40.bottom", {"start": v(185, 55) * mm, "end": v(95, 55) * mm});
            skLineSegment(sketch, "E40.top", {"start": v(185, -10) * mm, "end": v(95, -10) * mm});
            skLineSegment(sketch, "E40.left", {"start": v(185, 55) * mm, "end": v(185, -10) * mm});
            skLineSegment(sketch, "E40.right", {"start": v(95, 55) * mm, "end": v(95, -10) * mm});
            skSolve(sketch);
        }
        {
            var Q0;
            Q0 = qSketchRegion(id + "F6", true);
            var Q1;
            Q1=makeQuery(id+"F6.imprint","IMPRINT",FACE,{"disambiguationData":[TD([[makeQuery(id+"F6.imprint","IMPRINT",EDGE,{"derivedFrom":sQuery(id+"F6.wireOp",EDGE,"E40.bottom")}),1.0]])]});
            var Q2;
            Q2=makeQuery(id+"F6.imprint","IMPRINT",FACE,{"disambiguationData":[TD([[makeQuery(id+"F6.imprint","IMPRINT",EDGE,{"derivedFrom":sQuery(id+"F6.wireOp",EDGE,"E28.bottom")}),-1.0]])]});
            var Q3;
            Q3=makeQuery(id+"F6.imprint","IMPRINT",FACE,{"disambiguationData":[TD([[makeQuery(id+"F6.imprint","IMPRINT",EDGE,{"derivedFrom":sQuery(id+"F6.wireOp",EDGE,"E29.1.0.0")}),-1.0]])]});
            var Q4;
            {var subQ0=sQuery(id+"F6.wireOp",EDGE,"E29.0.1.0");Q4=makeQuery(id+"F6.imprint","IMPRINT",FACE,{"disambiguationData":[TD([[makeQuery(id+"F6.imprint","IMPRINT",EDGE,{"derivedFrom":subQ0}),-1.0]])]});}
            var Q5;
            Q5=makeQuery(id+"F6.imprint","IMPRINT",FACE,{"disambiguationData":[TD([[makeQuery(id+"F6.imprint","IMPRINT",EDGE,{"derivedFrom":sQuery(id+"F6.wireOp",EDGE,"E29.1.1.0")}),-1.0]])]});
            var Q6;
            Q6=makeQuery(id+"F6.imprint","IMPRINT",FACE,{"disambiguationData":[TD([[makeQuery(id+"F6.imprint","IMPRINT",EDGE,{"derivedFrom":sQuery(id+"F6.wireOp",EDGE,"E29.1.2.0")}),-1.0]])]});
            var Q7;
            {var subQ0=sQuery(id+"F6.wireOp",EDGE,"E29.0.2.0");Q7=makeQuery(id+"F6.imprint","IMPRINT",FACE,{"disambiguationData":[TD([[makeQuery(id+"F6.imprint","IMPRINT",EDGE,{"derivedFrom":subQ0}),-1.0]])]});}
            var Q8;
            {var subQ0=sQuery(id+"F6.wireOp",EDGE,"E29.0.3.0");Q8=makeQuery(id+"F6.imprint","IMPRINT",FACE,{"disambiguationData":[TD([[makeQuery(id+"F6.imprint","IMPRINT",EDGE,{"derivedFrom":subQ0}),-1.0]])]});}
            var Q9;
            Q9=makeQuery(id+"F6.imprint","IMPRINT",FACE,{"disambiguationData":[TD([[makeQuery(id+"F6.imprint","IMPRINT",EDGE,{"derivedFrom":sQuery(id+"F6.wireOp",EDGE,"E29.1.3.0")}),-1.0]])]});
            var Q10;
            Q10=makeQuery(id+"F6.imprint","IMPRINT",FACE,{"disambiguationData":[TD([[makeQuery(id+"F6.imprint","IMPRINT",EDGE,{"derivedFrom":sQuery(id+"F6.wireOp",EDGE,"E29.1.4.0")}),-1.0]])]});
            var Q11;
            {var subQ0=sQuery(id+"F6.wireOp",EDGE,"E29.0.4.0");Q11=makeQuery(id+"F6.imprint","IMPRINT",FACE,{"disambiguationData":[TD([[makeQuery(id+"F6.imprint","IMPRINT",EDGE,{"derivedFrom":subQ0}),-1.0]])]});}
            var Q12;
            {var subQ0=sQuery(id+"F6.wireOp",EDGE,"E29.0.5.0");Q12=makeQuery(id+"F6.imprint","IMPRINT",FACE,{"disambiguationData":[TD([[makeQuery(id+"F6.imprint","IMPRINT",EDGE,{"derivedFrom":subQ0}),-1.0]])]});}
            var Q13;
            {var subQ0=sQuery(id+"F6.wireOp",EDGE,"E29.0.6.0");Q13=makeQuery(id+"F6.imprint","IMPRINT",FACE,{"disambiguationData":[TD([[makeQuery(id+"F6.imprint","IMPRINT",EDGE,{"derivedFrom":subQ0}),-1.0]])]});}
            var Q14;
            {var subQ0=sQuery(id+"F6.wireOp",EDGE,"E29.0.7.0");Q14=makeQuery(id+"F6.imprint","IMPRINT",FACE,{"disambiguationData":[TD([[makeQuery(id+"F6.imprint","IMPRINT",EDGE,{"derivedFrom":subQ0}),-1.0]])]});}
            var Q15;
            {var subQ0=sQuery(id+"F6.wireOp",EDGE,"E30.0.1.0");Q15=makeQuery(id+"F6.imprint","IMPRINT",FACE,{"disambiguationData":[TD([[makeQuery(id+"F6.imprint","IMPRINT",EDGE,{"derivedFrom":subQ0}),1.0]])]});}
            var Q16;
            {var subQ0=sQuery(id+"F6.wireOp",EDGE,"E30.0.1.3");Q16=makeQuery(id+"F6.imprint","IMPRINT",FACE,{"disambiguationData":[TD([[makeQuery(id+"F6.imprint","IMPRINT",EDGE,{"derivedFrom":subQ0}),-1.0]])]});}
            var Q17;
            Q17=makeQuery(id+"F6.imprint","IMPRINT",FACE,{"disambiguationData":[TD([[makeQuery(id+"F6.imprint","IMPRINT",EDGE,{"derivedFrom":sQuery(id+"F6.wireOp",EDGE,"E29.1.7.0")}),-1.0]])]});
            var Q18;
            Q18=makeQuery(id+"F6.imprint","IMPRINT",FACE,{"disambiguationData":[TD([[makeQuery(id+"F6.imprint","IMPRINT",EDGE,{"derivedFrom":sQuery(id+"F6.wireOp",EDGE,"E29.1.6.0")}),-1.0]])]});
            var Q19;
            Q19=makeQuery(id+"F6.imprint","IMPRINT",FACE,{"disambiguationData":[TD([[makeQuery(id+"F6.imprint","IMPRINT",EDGE,{"derivedFrom":sQuery(id+"F6.wireOp",EDGE,"E29.1.5.0")}),-1.0]])]});
            extrude(context, id + "F7", {"entities" : qUnion([Q0, Q1, Q2, Q3, Q4, Q5, Q6, Q7, Q8, Q9, Q10, Q11, Q12, Q13, Q14, Q15, Q16, Q17, Q18, Q19]), "depth" : 3 * mm});
        }
        {
            var Q0;
            Q0=makeQuery(id+"F7.opExtrude","CAP_FACE",FACE,{"disambiguationData":[OSD([sQuery(id+"F6.wireOp",EDGE,"E16.0"),sQuery(id+"F6.wireOp",EDGE,"E17.0"),sQuery(id+"F6.wireOp",EDGE,"E18.0"),sQuery(id+"F6.wireOp",EDGE,"E19.0"),sQuery(id+"F6.wireOp",EDGE,"E20.0"),sQuery(id+"F6.wireOp",EDGE,"E25"),sQuery(id+"F6.wireOp",EDGE,"E26"),sQuery(id+"F6.wireOp",EDGE,"E27"),sQuery(id+"F6.wireOp",EDGE,"E28.bottom"),sQuery(id+"F6.wireOp",EDGE,"E28.top"),sQuery(id+"F6.wireOp",EDGE,"E28.right"),sQuery(id+"F6.wireOp",EDGE,"E29.0.1.0"),sQuery(id+"F6.wireOp",EDGE,"E29.0.1.1"),sQuery(id+"F6.wireOp",EDGE,"E29.0.1.2"),sQuery(id+"F6.wireOp",EDGE,"E29.0.2.0"),sQuery(id+"F6.wireOp",EDGE,"E29.0.2.1"),sQuery(id+"F6.wireOp",EDGE,"E29.0.2.2"),sQuery(id+"F6.wireOp",EDGE,"E29.0.3.0"),sQuery(id+"F6.wireOp",EDGE,"E29.0.3.1"),sQuery(id+"F6.wireOp",EDGE,"E29.0.3.2"),sQuery(id+"F6.wireOp",EDGE,"E29.0.4.0"),sQuery(id+"F6.wireOp",EDGE,"E29.0.4.1"),sQuery(id+"F6.wireOp",EDGE,"E29.0.4.2"),sQuery(id+"F6.wireOp",EDGE,"E29.0.5.0"),sQuery(id+"F6.wireOp",EDGE,"E29.0.5.1"),sQuery(id+"F6.wireOp",EDGE,"E29.0.5.2"),sQuery(id+"F6.wireOp",EDGE,"E29.0.6.0"),sQuery(id+"F6.wireOp",EDGE,"E29.0.6.1"),sQuery(id+"F6.wireOp",EDGE,"E29.0.6.2"),sQuery(id+"F6.wireOp",EDGE,"E29.0.7.0"),sQuery(id+"F6.wireOp",EDGE,"E29.0.7.1"),sQuery(id+"F6.wireOp",EDGE,"E29.0.7.2"),sQuery(id+"F6.wireOp",EDGE,"E29.1.0.0"),sQuery(id+"F6.wireOp",EDGE,"E29.1.0.1"),sQuery(id+"F6.wireOp",EDGE,"E29.1.1.0"),sQuery(id+"F6.wireOp",EDGE,"E29.1.1.1"),sQuery(id+"F6.wireOp",EDGE,"E29.1.2.0"),sQuery(id+"F6.wireOp",EDGE,"E29.1.2.1"),sQuery(id+"F6.wireOp",EDGE,"E29.1.3.0"),sQuery(id+"F6.wireOp",EDGE,"E29.1.3.1"),sQuery(id+"F6.wireOp",EDGE,"E29.1.4.0"),sQuery(id+"F6.wireOp",EDGE,"E29.1.4.1"),sQuery(id+"F6.wireOp",EDGE,"E29.1.5.0"),sQuery(id+"F6.wireOp",EDGE,"E29.1.5.1"),sQuery(id+"F6.wireOp",EDGE,"E29.1.6.0"),sQuery(id+"F6.wireOp",EDGE,"E29.1.6.1"),sQuery(id+"F6.wireOp",EDGE,"E29.1.7.0"),sQuery(id+"F6.wireOp",EDGE,"E29.1.7.1"),sQuery(id+"F6.wireOp",EDGE,"E30.0.1.0"),sQuery(id+"F6.wireOp",EDGE,"E30.0.1.1"),sQuery(id+"F6.wireOp",EDGE,"E30.0.1.2"),sQuery(id+"F6.wireOp",EDGE,"E30.0.1.3"),sQuery(id+"F6.wireOp",EDGE,"E30.0.1.4"),sQuery(id+"F6.wireOp",EDGE,"E31"),sQuery(id+"F6.wireOp",EDGE,"E32"),sQuery(id+"F6.wireOp",EDGE,"E33"),sQuery(id+"F6.wireOp",EDGE,"E34"),sQuery(id+"F6.wireOp",EDGE,"E35"),sQuery(id+"F6.wireOp",EDGE,"E36"),sQuery(id+"F6.wireOp",EDGE,"E37"),sQuery(id+"F6.wireOp",EDGE,"E38"),sQuery(id+"F6.wireOp",EDGE,"E39"),sQuery(id+"F6.wireOp",EDGE,"E40.top"),sQuery(id+"F6.wireOp",EDGE,"E40.right")])],"isStart":false});
            var sketch = newSketch(context, id + "F8", { "sketchPlane" : qUnion([Q0])});
            skLineSegment(sketch, "E41.bottom", {"start": v(-10, 95) * mm, "end": v(210, 95) * mm});
            skLineSegment(sketch, "E41.top", {"start": v(-10, -290) * mm, "end": v(210, -290) * mm});
            skLineSegment(sketch, "E41.left", {"start": v(-10, 95) * mm, "end": v(-10, -290) * mm});
            skLineSegment(sketch, "E41.right", {"start": v(210, 95) * mm, "end": v(210, -290) * mm});
            skSolve(sketch);
        }
        {
            var Q0;
            Q0 = qSketchRegion(id + "F8", true);
            extrude(context, id + "F9", {"entities" : qUnion([Q0]), "depth" : 3 * mm});
        }
        {
            var Q0;
            Q0=makeQuery(id+"F2.imprint","IMPRINT",FACE,{"disambiguationData":[TD([[makeQuery(id+"F2.imprint","IMPRINT",EDGE,{"derivedFrom":sQuery(id+"F2.wireOp",EDGE,"E11")}),1.0]])]});
            extrude(context, id + "F10", {"entities" : qUnion([Q0]), "oppositeDirection" : true, "depth" : 3 * mm});
        }
        {
            var Q0;
            Q0=makeQuery(id+"F2.imprint","IMPRINT",FACE,{"disambiguationData":[TD([[makeQuery(id+"F2.imprint","IMPRINT",EDGE,{"derivedFrom":sQuery(id+"F2.wireOp",EDGE,"E11")}),1.0]])]});
            var sketch = newSketch(context, id + "F11", { "sketchPlane" : qUnion([Q0])});
            skLineSegment(sketch, "E42.bottom", {"start": v(59.57, -10) * mm, "end": v(4.57, -10) * mm});
            skLineSegment(sketch, "E42.top", {"start": v(59.57, -65) * mm, "end": v(4.57, -65) * mm});
            skLineSegment(sketch, "E42.left", {"start": v(59.57, -10) * mm, "end": v(59.57, -65) * mm});
            skLineSegment(sketch, "E42.right", {"start": v(4.57, -10) * mm, "end": v(4.57, -65) * mm});
            skSolve(sketch);
        }
        {
            var Q0;
            Q0 = qSketchRegion(id + "F11", true);
            extrude(context, id + "F12", {"entities" : qUnion([Q0]), "operationType" : NewBodyOperationType.ADD, "depth" : 3 * mm});
        }
        {
            var Q0;
            Q0=makeQuery(id+"F12.opExtrude","CAP_FACE",FACE,{"disambiguationData":[OSD([sQuery(id+"F11.wireOp",EDGE,"E42.bottom"),sQuery(id+"F11.wireOp",EDGE,"E42.top"),sQuery(id+"F11.wireOp",EDGE,"E42.left"),sQuery(id+"F11.wireOp",EDGE,"E42.right")])],"isStart":false});
            var sketch = newSketch(context, id + "F13", { "sketchPlane" : qUnion([Q0])});
            skCircle(sketch, "E43", {"center": v(32.07, -37.07) * mm, "radius": 6.25 * mm});
            skSolve(sketch);
        }
        {
            var Q0;
            Q0=makeQuery(id+"F13.imprint","IMPRINT",FACE,{"disambiguationData":[TD([[makeQuery(id+"F13.imprint","IMPRINT",EDGE,{"derivedFrom":sQuery(id+"F13.wireOp",EDGE,"E43")}),1.0]])]});
            extrude(context, id + "F14", {"entities" : qUnion([Q0]), "operationType" : NewBodyOperationType.REMOVE, "endBound" : BoundingType.THROUGH_ALL, "oppositeDirection" : true, "depth" : 25 * mm});
        }
        {
            var Q0;
            Q0=makeQuery(id+"F2.imprint","IMPRINT",FACE,{"disambiguationData":[TD([[makeQuery(id+"F2.imprint","IMPRINT",EDGE,{"derivedFrom":sQuery(id+"F2.wireOp",EDGE,"E2.0")}),-1.0]])]});
            var sketch = newSketch(context, id + "F15", { "sketchPlane" : qUnion([Q0])});
            skLineSegment(sketch, "E44.0", {"start": v(0, 250) * mm, "end": v(200, 250) * mm});
            skLineSegment(sketch, "E45.0", {"start": v(0, 0) * mm, "end": v(0, 250) * mm});
            skLineSegment(sketch, "E46.0", {"start": v(0, 0) * mm, "end": v(200, 0) * mm});
            skLineSegment(sketch, "E47.0", {"start": v(200, 0) * mm, "end": v(200, 250) * mm});
            skLineSegment(sketch, "E48.bottom", {"start": v(56.65, 240) * mm, "end": v(131.65, 240) * mm});
            skLineSegment(sketch, "E48.top", {"start": v(56.65, 140) * mm, "end": v(131.65, 140) * mm});
            skLineSegment(sketch, "E48.left", {"start": v(56.65, 240) * mm, "end": v(56.65, 140) * mm});
            skLineSegment(sketch, "E48.right", {"start": v(131.65, 240) * mm, "end": v(131.65, 140) * mm});
            skPoint(sketch, "E49", {"position": v(94.15, 240) * mm});
            skSolve(sketch);
        }
        {
            var Q0;
            Q0 = qSketchRegion(id + "F15", true);
            extrude(context, id + "F16", {"entities" : qUnion([Q0]), "depth" : 1 * mm});
        }
        {
            var Q0;
            Q0=makeQuery(id+"F5.opExtrude","CAP_FACE",FACE,{"disambiguationData":[OSD([sQuery(id+"F4.wireOp",EDGE,"E12.0.0"),sQuery(id+"F4.wireOp",EDGE,"E12.0.1"),sQuery(id+"F4.wireOp",EDGE,"E12.0.2"),sQuery(id+"F4.wireOp",EDGE,"E12.0.3"),sQuery(id+"F4.wireOp",EDGE,"E13.0"),sQuery(id+"F4.wireOp",EDGE,"E14"),sQuery(id+"F4.wireOp",EDGE,"E15.0.1.0"),sQuery(id+"F4.wireOp",EDGE,"E15.0.2.0"),sQuery(id+"F4.wireOp",EDGE,"E15.0.3.0"),sQuery(id+"F4.wireOp",EDGE,"E15.0.4.0"),sQuery(id+"F4.wireOp",EDGE,"E15.0.5.0"),sQuery(id+"F4.wireOp",EDGE,"E15.0.6.0"),sQuery(id+"F4.wireOp",EDGE,"E15.0.7.0"),sQuery(id+"F4.wireOp",EDGE,"E15.0.8.0"),sQuery(id+"F4.wireOp",EDGE,"E15.0.9.0"),sQuery(id+"F4.wireOp",EDGE,"E15.0.10.0"),sQuery(id+"F4.wireOp",EDGE,"E15.0.11.0"),sQuery(id+"F4.wireOp",EDGE,"E15.0.12.0"),sQuery(id+"F4.wireOp",EDGE,"E15.0.13.0"),sQuery(id+"F4.wireOp",EDGE,"E15.0.14.0"),sQuery(id+"F4.wireOp",EDGE,"E15.0.15.0"),sQuery(id+"F4.wireOp",EDGE,"E15.0.16.0"),sQuery(id+"F4.wireOp",EDGE,"E15.0.17.0"),sQuery(id+"F4.wireOp",EDGE,"E15.0.18.0"),sQuery(id+"F4.wireOp",EDGE,"E15.0.19.0"),sQuery(id+"F4.wireOp",EDGE,"E15.0.20.0"),sQuery(id+"F4.wireOp",EDGE,"E15.1.0.0"),sQuery(id+"F4.wireOp",EDGE,"E15.1.1.0"),sQuery(id+"F4.wireOp",EDGE,"E15.1.2.0"),sQuery(id+"F4.wireOp",EDGE,"E15.1.3.0"),sQuery(id+"F4.wireOp",EDGE,"E15.1.4.0"),sQuery(id+"F4.wireOp",EDGE,"E15.1.5.0"),sQuery(id+"F4.wireOp",EDGE,"E15.1.6.0"),sQuery(id+"F4.wireOp",EDGE,"E15.1.7.0"),sQuery(id+"F4.wireOp",EDGE,"E15.1.8.0"),sQuery(id+"F4.wireOp",EDGE,"E15.1.9.0"),sQuery(id+"F4.wireOp",EDGE,"E15.1.10.0"),sQuery(id+"F4.wireOp",EDGE,"E15.1.11.0"),sQuery(id+"F4.wireOp",EDGE,"E15.1.12.0"),sQuery(id+"F4.wireOp",EDGE,"E15.1.13.0"),sQuery(id+"F4.wireOp",EDGE,"E15.1.14.0"),sQuery(id+"F4.wireOp",EDGE,"E15.1.15.0"),sQuery(id+"F4.wireOp",EDGE,"E15.1.16.0"),sQuery(id+"F4.wireOp",EDGE,"E15.1.17.0"),sQuery(id+"F4.wireOp",EDGE,"E15.1.18.0"),sQuery(id+"F4.wireOp",EDGE,"E15.1.19.0"),sQuery(id+"F4.wireOp",EDGE,"E15.1.20.0"),sQuery(id+"F4.wireOp",EDGE,"E15.2.0.0"),sQuery(id+"F4.wireOp",EDGE,"E15.2.1.0"),sQuery(id+"F4.wireOp",EDGE,"E15.2.2.0"),sQuery(id+"F4.wireOp",EDGE,"E15.2.3.0"),sQuery(id+"F4.wireOp",EDGE,"E15.2.4.0"),sQuery(id+"F4.wireOp",EDGE,"E15.2.5.0"),sQuery(id+"F4.wireOp",EDGE,"E15.2.6.0"),sQuery(id+"F4.wireOp",EDGE,"E15.2.7.0"),sQuery(id+"F4.wireOp",EDGE,"E15.2.8.0"),sQuery(id+"F4.wireOp",EDGE,"E15.2.9.0"),sQuery(id+"F4.wireOp",EDGE,"E15.2.10.0"),sQuery(id+"F4.wireOp",EDGE,"E15.2.11.0"),sQuery(id+"F4.wireOp",EDGE,"E15.2.12.0"),sQuery(id+"F4.wireOp",EDGE,"E15.2.13.0"),sQuery(id+"F4.wireOp",EDGE,"E15.2.14.0"),sQuery(id+"F4.wireOp",EDGE,"E15.2.15.0"),sQuery(id+"F4.wireOp",EDGE,"E15.2.16.0"),sQuery(id+"F4.wireOp",EDGE,"E15.2.17.0"),sQuery(id+"F4.wireOp",EDGE,"E15.2.18.0"),sQuery(id+"F4.wireOp",EDGE,"E15.2.19.0"),sQuery(id+"F4.wireOp",EDGE,"E15.2.20.0"),sQuery(id+"F4.wireOp",EDGE,"E15.3.0.0"),sQuery(id+"F4.wireOp",EDGE,"E15.3.1.0"),sQuery(id+"F4.wireOp",EDGE,"E15.3.2.0"),sQuery(id+"F4.wireOp",EDGE,"E15.3.3.0"),sQuery(id+"F4.wireOp",EDGE,"E15.3.4.0"),sQuery(id+"F4.wireOp",EDGE,"E15.3.5.0"),sQuery(id+"F4.wireOp",EDGE,"E15.3.6.0"),sQuery(id+"F4.wireOp",EDGE,"E15.3.7.0"),sQuery(id+"F4.wireOp",EDGE,"E15.3.8.0"),sQuery(id+"F4.wireOp",EDGE,"E15.3.9.0"),sQuery(id+"F4.wireOp",EDGE,"E15.3.10.0"),sQuery(id+"F4.wireOp",EDGE,"E15.3.11.0"),sQuery(id+"F4.wireOp",EDGE,"E15.3.12.0"),sQuery(id+"F4.wireOp",EDGE,"E15.3.13.0"),sQuery(id+"F4.wireOp",EDGE,"E15.3.14.0"),sQuery(id+"F4.wireOp",EDGE,"E15.3.15.0"),sQuery(id+"F4.wireOp",EDGE,"E15.3.16.0"),sQuery(id+"F4.wireOp",EDGE,"E15.3.17.0"),sQuery(id+"F4.wireOp",EDGE,"E15.3.18.0"),sQuery(id+"F4.wireOp",EDGE,"E15.3.19.0"),sQuery(id+"F4.wireOp",EDGE,"E15.3.20.0"),sQuery(id+"F4.wireOp",EDGE,"E15.4.0.0"),sQuery(id+"F4.wireOp",EDGE,"E15.4.1.0"),sQuery(id+"F4.wireOp",EDGE,"E15.4.2.0"),sQuery(id+"F4.wireOp",EDGE,"E15.4.3.0"),sQuery(id+"F4.wireOp",EDGE,"E15.4.4.0"),sQuery(id+"F4.wireOp",EDGE,"E15.4.5.0"),sQuery(id+"F4.wireOp",EDGE,"E15.4.6.0"),sQuery(id+"F4.wireOp",EDGE,"E15.4.7.0"),sQuery(id+"F4.wireOp",EDGE,"E15.4.8.0"),sQuery(id+"F4.wireOp",EDGE,"E15.4.9.0"),sQuery(id+"F4.wireOp",EDGE,"E15.4.10.0"),sQuery(id+"F4.wireOp",EDGE,"E15.4.11.0"),sQuery(id+"F4.wireOp",EDGE,"E15.4.12.0"),sQuery(id+"F4.wireOp",EDGE,"E15.4.13.0"),sQuery(id+"F4.wireOp",EDGE,"E15.4.14.0"),sQuery(id+"F4.wireOp",EDGE,"E15.4.15.0"),sQuery(id+"F4.wireOp",EDGE,"E15.4.16.0"),sQuery(id+"F4.wireOp",EDGE,"E15.4.17.0"),sQuery(id+"F4.wireOp",EDGE,"E15.4.18.0"),sQuery(id+"F4.wireOp",EDGE,"E15.4.19.0"),sQuery(id+"F4.wireOp",EDGE,"E15.4.20.0"),sQuery(id+"F4.wireOp",EDGE,"E15.5.0.0"),sQuery(id+"F4.wireOp",EDGE,"E15.5.1.0"),sQuery(id+"F4.wireOp",EDGE,"E15.5.2.0"),sQuery(id+"F4.wireOp",EDGE,"E15.5.3.0"),sQuery(id+"F4.wireOp",EDGE,"E15.5.4.0"),sQuery(id+"F4.wireOp",EDGE,"E15.5.5.0"),sQuery(id+"F4.wireOp",EDGE,"E15.5.6.0"),sQuery(id+"F4.wireOp",EDGE,"E15.5.7.0"),sQuery(id+"F4.wireOp",EDGE,"E15.5.8.0"),sQuery(id+"F4.wireOp",EDGE,"E15.5.9.0"),sQuery(id+"F4.wireOp",EDGE,"E15.5.10.0"),sQuery(id+"F4.wireOp",EDGE,"E15.5.11.0"),sQuery(id+"F4.wireOp",EDGE,"E15.5.12.0"),sQuery(id+"F4.wireOp",EDGE,"E15.5.13.0"),sQuery(id+"F4.wireOp",EDGE,"E15.5.14.0"),sQuery(id+"F4.wireOp",EDGE,"E15.5.15.0"),sQuery(id+"F4.wireOp",EDGE,"E15.5.16.0"),sQuery(id+"F4.wireOp",EDGE,"E15.5.17.0"),sQuery(id+"F4.wireOp",EDGE,"E15.5.18.0"),sQuery(id+"F4.wireOp",EDGE,"E15.5.19.0"),sQuery(id+"F4.wireOp",EDGE,"E15.5.20.0"),sQuery(id+"F4.wireOp",EDGE,"E15.6.0.0"),sQuery(id+"F4.wireOp",EDGE,"E15.6.1.0"),sQuery(id+"F4.wireOp",EDGE,"E15.6.2.0"),sQuery(id+"F4.wireOp",EDGE,"E15.6.3.0"),sQuery(id+"F4.wireOp",EDGE,"E15.6.4.0"),sQuery(id+"F4.wireOp",EDGE,"E15.6.5.0"),sQuery(id+"F4.wireOp",EDGE,"E15.6.6.0"),sQuery(id+"F4.wireOp",EDGE,"E15.6.7.0"),sQuery(id+"F4.wireOp",EDGE,"E15.6.8.0"),sQuery(id+"F4.wireOp",EDGE,"E15.6.9.0"),sQuery(id+"F4.wireOp",EDGE,"E15.6.10.0"),sQuery(id+"F4.wireOp",EDGE,"E15.6.11.0"),sQuery(id+"F4.wireOp",EDGE,"E15.6.12.0"),sQuery(id+"F4.wireOp",EDGE,"E15.6.13.0"),sQuery(id+"F4.wireOp",EDGE,"E15.6.14.0"),sQuery(id+"F4.wireOp",EDGE,"E15.6.15.0"),sQuery(id+"F4.wireOp",EDGE,"E15.6.16.0"),sQuery(id+"F4.wireOp",EDGE,"E15.6.17.0"),sQuery(id+"F4.wireOp",EDGE,"E15.6.18.0"),sQuery(id+"F4.wireOp",EDGE,"E15.6.19.0"),sQuery(id+"F4.wireOp",EDGE,"E15.6.20.0"),sQuery(id+"F4.wireOp",EDGE,"E15.7.0.0"),sQuery(id+"F4.wireOp",EDGE,"E15.7.1.0"),sQuery(id+"F4.wireOp",EDGE,"E15.7.2.0"),sQuery(id+"F4.wireOp",EDGE,"E15.7.3.0"),sQuery(id+"F4.wireOp",EDGE,"E15.7.4.0"),sQuery(id+"F4.wireOp",EDGE,"E15.7.5.0"),sQuery(id+"F4.wireOp",EDGE,"E15.7.6.0"),sQuery(id+"F4.wireOp",EDGE,"E15.7.7.0"),sQuery(id+"F4.wireOp",EDGE,"E15.7.8.0"),sQuery(id+"F4.wireOp",EDGE,"E15.7.9.0"),sQuery(id+"F4.wireOp",EDGE,"E15.7.10.0"),sQuery(id+"F4.wireOp",EDGE,"E15.7.11.0"),sQuery(id+"F4.wireOp",EDGE,"E15.7.12.0"),sQuery(id+"F4.wireOp",EDGE,"E15.7.13.0"),sQuery(id+"F4.wireOp",EDGE,"E15.7.14.0"),sQuery(id+"F4.wireOp",EDGE,"E15.7.15.0"),sQuery(id+"F4.wireOp",EDGE,"E15.7.16.0"),sQuery(id+"F4.wireOp",EDGE,"E15.7.17.0"),sQuery(id+"F4.wireOp",EDGE,"E15.7.18.0"),sQuery(id+"F4.wireOp",EDGE,"E15.7.19.0"),sQuery(id+"F4.wireOp",EDGE,"E15.7.20.0"),sQuery(id+"F4.wireOp",EDGE,"E15.8.0.0"),sQuery(id+"F4.wireOp",EDGE,"E15.8.1.0"),sQuery(id+"F4.wireOp",EDGE,"E15.8.2.0"),sQuery(id+"F4.wireOp",EDGE,"E15.8.3.0"),sQuery(id+"F4.wireOp",EDGE,"E15.8.4.0"),sQuery(id+"F4.wireOp",EDGE,"E15.8.5.0"),sQuery(id+"F4.wireOp",EDGE,"E15.8.6.0"),sQuery(id+"F4.wireOp",EDGE,"E15.8.7.0"),sQuery(id+"F4.wireOp",EDGE,"E15.8.8.0"),sQuery(id+"F4.wireOp",EDGE,"E15.8.9.0"),sQuery(id+"F4.wireOp",EDGE,"E15.8.10.0"),sQuery(id+"F4.wireOp",EDGE,"E15.8.11.0"),sQuery(id+"F4.wireOp",EDGE,"E15.8.12.0"),sQuery(id+"F4.wireOp",EDGE,"E15.8.13.0"),sQuery(id+"F4.wireOp",EDGE,"E15.8.14.0"),sQuery(id+"F4.wireOp",EDGE,"E15.8.15.0"),sQuery(id+"F4.wireOp",EDGE,"E15.8.16.0"),sQuery(id+"F4.wireOp",EDGE,"E15.8.17.0"),sQuery(id+"F4.wireOp",EDGE,"E15.8.18.0"),sQuery(id+"F4.wireOp",EDGE,"E15.8.19.0"),sQuery(id+"F4.wireOp",EDGE,"E15.8.20.0"),sQuery(id+"F4.wireOp",EDGE,"E15.9.0.0"),sQuery(id+"F4.wireOp",EDGE,"E15.9.1.0"),sQuery(id+"F4.wireOp",EDGE,"E15.9.2.0"),sQuery(id+"F4.wireOp",EDGE,"E15.9.3.0"),sQuery(id+"F4.wireOp",EDGE,"E15.9.4.0"),sQuery(id+"F4.wireOp",EDGE,"E15.9.5.0"),sQuery(id+"F4.wireOp",EDGE,"E15.9.6.0"),sQuery(id+"F4.wireOp",EDGE,"E15.9.7.0"),sQuery(id+"F4.wireOp",EDGE,"E15.9.8.0"),sQuery(id+"F4.wireOp",EDGE,"E15.9.9.0"),sQuery(id+"F4.wireOp",EDGE,"E15.9.10.0"),sQuery(id+"F4.wireOp",EDGE,"E15.9.11.0"),sQuery(id+"F4.wireOp",EDGE,"E15.9.12.0"),sQuery(id+"F4.wireOp",EDGE,"E15.9.13.0"),sQuery(id+"F4.wireOp",EDGE,"E15.9.14.0"),sQuery(id+"F4.wireOp",EDGE,"E15.9.15.0"),sQuery(id+"F4.wireOp",EDGE,"E15.9.16.0"),sQuery(id+"F4.wireOp",EDGE,"E15.9.17.0"),sQuery(id+"F4.wireOp",EDGE,"E15.9.18.0"),sQuery(id+"F4.wireOp",EDGE,"E15.9.19.0"),sQuery(id+"F4.wireOp",EDGE,"E15.9.20.0"),sQuery(id+"F4.wireOp",EDGE,"E15.10.0.0"),sQuery(id+"F4.wireOp",EDGE,"E15.10.1.0"),sQuery(id+"F4.wireOp",EDGE,"E15.10.2.0"),sQuery(id+"F4.wireOp",EDGE,"E15.10.3.0"),sQuery(id+"F4.wireOp",EDGE,"E15.10.4.0"),sQuery(id+"F4.wireOp",EDGE,"E15.10.5.0"),sQuery(id+"F4.wireOp",EDGE,"E15.10.6.0"),sQuery(id+"F4.wireOp",EDGE,"E15.10.7.0"),sQuery(id+"F4.wireOp",EDGE,"E15.10.8.0"),sQuery(id+"F4.wireOp",EDGE,"E15.10.9.0"),sQuery(id+"F4.wireOp",EDGE,"E15.10.10.0"),sQuery(id+"F4.wireOp",EDGE,"E15.10.11.0"),sQuery(id+"F4.wireOp",EDGE,"E15.10.12.0"),sQuery(id+"F4.wireOp",EDGE,"E15.10.13.0"),sQuery(id+"F4.wireOp",EDGE,"E15.10.14.0"),sQuery(id+"F4.wireOp",EDGE,"E15.10.15.0"),sQuery(id+"F4.wireOp",EDGE,"E15.10.16.0"),sQuery(id+"F4.wireOp",EDGE,"E15.10.17.0"),sQuery(id+"F4.wireOp",EDGE,"E15.10.18.0"),sQuery(id+"F4.wireOp",EDGE,"E15.10.19.0"),sQuery(id+"F4.wireOp",EDGE,"E15.10.20.0"),sQuery(id+"F4.wireOp",EDGE,"E15.11.0.0"),sQuery(id+"F4.wireOp",EDGE,"E15.11.1.0"),sQuery(id+"F4.wireOp",EDGE,"E15.11.2.0"),sQuery(id+"F4.wireOp",EDGE,"E15.11.3.0"),sQuery(id+"F4.wireOp",EDGE,"E15.11.4.0"),sQuery(id+"F4.wireOp",EDGE,"E15.11.5.0"),sQuery(id+"F4.wireOp",EDGE,"E15.11.6.0"),sQuery(id+"F4.wireOp",EDGE,"E15.11.7.0"),sQuery(id+"F4.wireOp",EDGE,"E15.11.8.0"),sQuery(id+"F4.wireOp",EDGE,"E15.11.9.0"),sQuery(id+"F4.wireOp",EDGE,"E15.11.10.0"),sQuery(id+"F4.wireOp",EDGE,"E15.11.11.0"),sQuery(id+"F4.wireOp",EDGE,"E15.11.12.0"),sQuery(id+"F4.wireOp",EDGE,"E15.11.13.0"),sQuery(id+"F4.wireOp",EDGE,"E15.11.14.0"),sQuery(id+"F4.wireOp",EDGE,"E15.11.15.0"),sQuery(id+"F4.wireOp",EDGE,"E15.11.16.0"),sQuery(id+"F4.wireOp",EDGE,"E15.11.17.0"),sQuery(id+"F4.wireOp",EDGE,"E15.11.18.0"),sQuery(id+"F4.wireOp",EDGE,"E15.11.19.0"),sQuery(id+"F4.wireOp",EDGE,"E15.11.20.0"),sQuery(id+"F4.wireOp",EDGE,"E15.12.0.0"),sQuery(id+"F4.wireOp",EDGE,"E15.12.1.0"),sQuery(id+"F4.wireOp",EDGE,"E15.12.2.0"),sQuery(id+"F4.wireOp",EDGE,"E15.12.3.0"),sQuery(id+"F4.wireOp",EDGE,"E15.12.4.0"),sQuery(id+"F4.wireOp",EDGE,"E15.12.5.0"),sQuery(id+"F4.wireOp",EDGE,"E15.12.6.0"),sQuery(id+"F4.wireOp",EDGE,"E15.12.7.0"),sQuery(id+"F4.wireOp",EDGE,"E15.12.8.0"),sQuery(id+"F4.wireOp",EDGE,"E15.12.9.0"),sQuery(id+"F4.wireOp",EDGE,"E15.12.10.0"),sQuery(id+"F4.wireOp",EDGE,"E15.12.11.0"),sQuery(id+"F4.wireOp",EDGE,"E15.12.12.0"),sQuery(id+"F4.wireOp",EDGE,"E15.12.13.0"),sQuery(id+"F4.wireOp",EDGE,"E15.12.14.0"),sQuery(id+"F4.wireOp",EDGE,"E15.12.15.0"),sQuery(id+"F4.wireOp",EDGE,"E15.12.16.0"),sQuery(id+"F4.wireOp",EDGE,"E15.12.17.0"),sQuery(id+"F4.wireOp",EDGE,"E15.12.18.0"),sQuery(id+"F4.wireOp",EDGE,"E15.12.19.0"),sQuery(id+"F4.wireOp",EDGE,"E15.12.20.0"),sQuery(id+"F4.wireOp",EDGE,"E15.13.0.0"),sQuery(id+"F4.wireOp",EDGE,"E15.13.1.0"),sQuery(id+"F4.wireOp",EDGE,"E15.13.2.0"),sQuery(id+"F4.wireOp",EDGE,"E15.13.3.0"),sQuery(id+"F4.wireOp",EDGE,"E15.13.4.0"),sQuery(id+"F4.wireOp",EDGE,"E15.13.5.0"),sQuery(id+"F4.wireOp",EDGE,"E15.13.6.0"),sQuery(id+"F4.wireOp",EDGE,"E15.13.7.0"),sQuery(id+"F4.wireOp",EDGE,"E15.13.8.0"),sQuery(id+"F4.wireOp",EDGE,"E15.13.9.0"),sQuery(id+"F4.wireOp",EDGE,"E15.13.10.0"),sQuery(id+"F4.wireOp",EDGE,"E15.13.11.0"),sQuery(id+"F4.wireOp",EDGE,"E15.13.12.0"),sQuery(id+"F4.wireOp",EDGE,"E15.13.13.0"),sQuery(id+"F4.wireOp",EDGE,"E15.13.14.0"),sQuery(id+"F4.wireOp",EDGE,"E15.13.15.0"),sQuery(id+"F4.wireOp",EDGE,"E15.13.16.0"),sQuery(id+"F4.wireOp",EDGE,"E15.13.17.0"),sQuery(id+"F4.wireOp",EDGE,"E15.13.18.0"),sQuery(id+"F4.wireOp",EDGE,"E15.13.19.0"),sQuery(id+"F4.wireOp",EDGE,"E15.13.20.0"),sQuery(id+"F4.wireOp",EDGE,"E15.14.0.0"),sQuery(id+"F4.wireOp",EDGE,"E15.14.1.0"),sQuery(id+"F4.wireOp",EDGE,"E15.14.2.0"),sQuery(id+"F4.wireOp",EDGE,"E15.14.3.0"),sQuery(id+"F4.wireOp",EDGE,"E15.14.4.0"),sQuery(id+"F4.wireOp",EDGE,"E15.14.5.0"),sQuery(id+"F4.wireOp",EDGE,"E15.14.6.0"),sQuery(id+"F4.wireOp",EDGE,"E15.14.7.0"),sQuery(id+"F4.wireOp",EDGE,"E15.14.8.0"),sQuery(id+"F4.wireOp",EDGE,"E15.14.9.0"),sQuery(id+"F4.wireOp",EDGE,"E15.14.10.0"),sQuery(id+"F4.wireOp",EDGE,"E15.14.11.0"),sQuery(id+"F4.wireOp",EDGE,"E15.14.12.0"),sQuery(id+"F4.wireOp",EDGE,"E15.14.13.0"),sQuery(id+"F4.wireOp",EDGE,"E15.14.14.0"),sQuery(id+"F4.wireOp",EDGE,"E15.14.15.0"),sQuery(id+"F4.wireOp",EDGE,"E15.14.16.0"),sQuery(id+"F4.wireOp",EDGE,"E15.14.17.0"),sQuery(id+"F4.wireOp",EDGE,"E15.14.18.0"),sQuery(id+"F4.wireOp",EDGE,"E15.14.19.0"),sQuery(id+"F4.wireOp",EDGE,"E15.14.20.0"),sQuery(id+"F4.wireOp",EDGE,"E15.15.0.0"),sQuery(id+"F4.wireOp",EDGE,"E15.15.1.0"),sQuery(id+"F4.wireOp",EDGE,"E15.15.2.0"),sQuery(id+"F4.wireOp",EDGE,"E15.15.3.0"),sQuery(id+"F4.wireOp",EDGE,"E15.15.4.0"),sQuery(id+"F4.wireOp",EDGE,"E15.15.5.0"),sQuery(id+"F4.wireOp",EDGE,"E15.15.6.0"),sQuery(id+"F4.wireOp",EDGE,"E15.15.7.0"),sQuery(id+"F4.wireOp",EDGE,"E15.15.8.0"),sQuery(id+"F4.wireOp",EDGE,"E15.15.9.0"),sQuery(id+"F4.wireOp",EDGE,"E15.15.10.0"),sQuery(id+"F4.wireOp",EDGE,"E15.15.11.0"),sQuery(id+"F4.wireOp",EDGE,"E15.15.12.0"),sQuery(id+"F4.wireOp",EDGE,"E15.15.13.0"),sQuery(id+"F4.wireOp",EDGE,"E15.15.14.0"),sQuery(id+"F4.wireOp",EDGE,"E15.15.15.0"),sQuery(id+"F4.wireOp",EDGE,"E15.15.16.0"),sQuery(id+"F4.wireOp",EDGE,"E15.15.17.0"),sQuery(id+"F4.wireOp",EDGE,"E15.15.18.0"),sQuery(id+"F4.wireOp",EDGE,"E15.15.19.0"),sQuery(id+"F4.wireOp",EDGE,"E15.15.20.0")])],"isStart":true});
            var sketch = newSketch(context, id + "F17", { "sketchPlane" : qUnion([Q0])});
            skLineSegment(sketch, "E50.0", {"start": v(-2.5, 252.5) * mm, "end": v(-2.5, -4.5) * mm});
            skLineSegment(sketch, "E50.1", {"start": v(202.5, 252.5) * mm, "end": v(-2.5, 252.5) * mm});
            skLineSegment(sketch, "E50.2", {"start": v(202.5, 252.5) * mm, "end": v(202.5, -4.5) * mm});
            skLineSegment(sketch, "E51", {"start": v(-2.5, -4.5) * mm, "end": v(202.5, -4.5) * mm});
            skCircle(sketch, "E52", {"center": v(-2.5, 252.5) * mm, "radius": 2.5 * mm});
            skCircle(sketch, "E53.0.1.0", {"center": v(-2.5, -4.5) * mm, "radius": 2.5 * mm});
            skCircle(sketch, "E53.1.0.0", {"center": v(202.5, 252.5) * mm, "radius": 2.5 * mm});
            skCircle(sketch, "E53.1.1.0", {"center": v(202.5, -4.5) * mm, "radius": 2.5 * mm});
            skLineSegment(sketch, "E53.direction1", {"start": v(-2.5, 252.5) * mm, "end": v(202.5, 252.5) * mm, "construction": true});
            skLineSegment(sketch, "E53.direction2", {"start": v(-2.5, 252.5) * mm, "end": v(-2.5, -4.5) * mm, "construction": true});
            skSolve(sketch);
        }
        {
            var Q0;
            Q0 = qSketchRegion(id + "F17", true);
            extrude(context, id + "F18", {"entities" : qUnion([Q0]), "operationType" : NewBodyOperationType.REMOVE, "oppositeDirection" : true, "depth" : 1 * mm});
        }
    });
